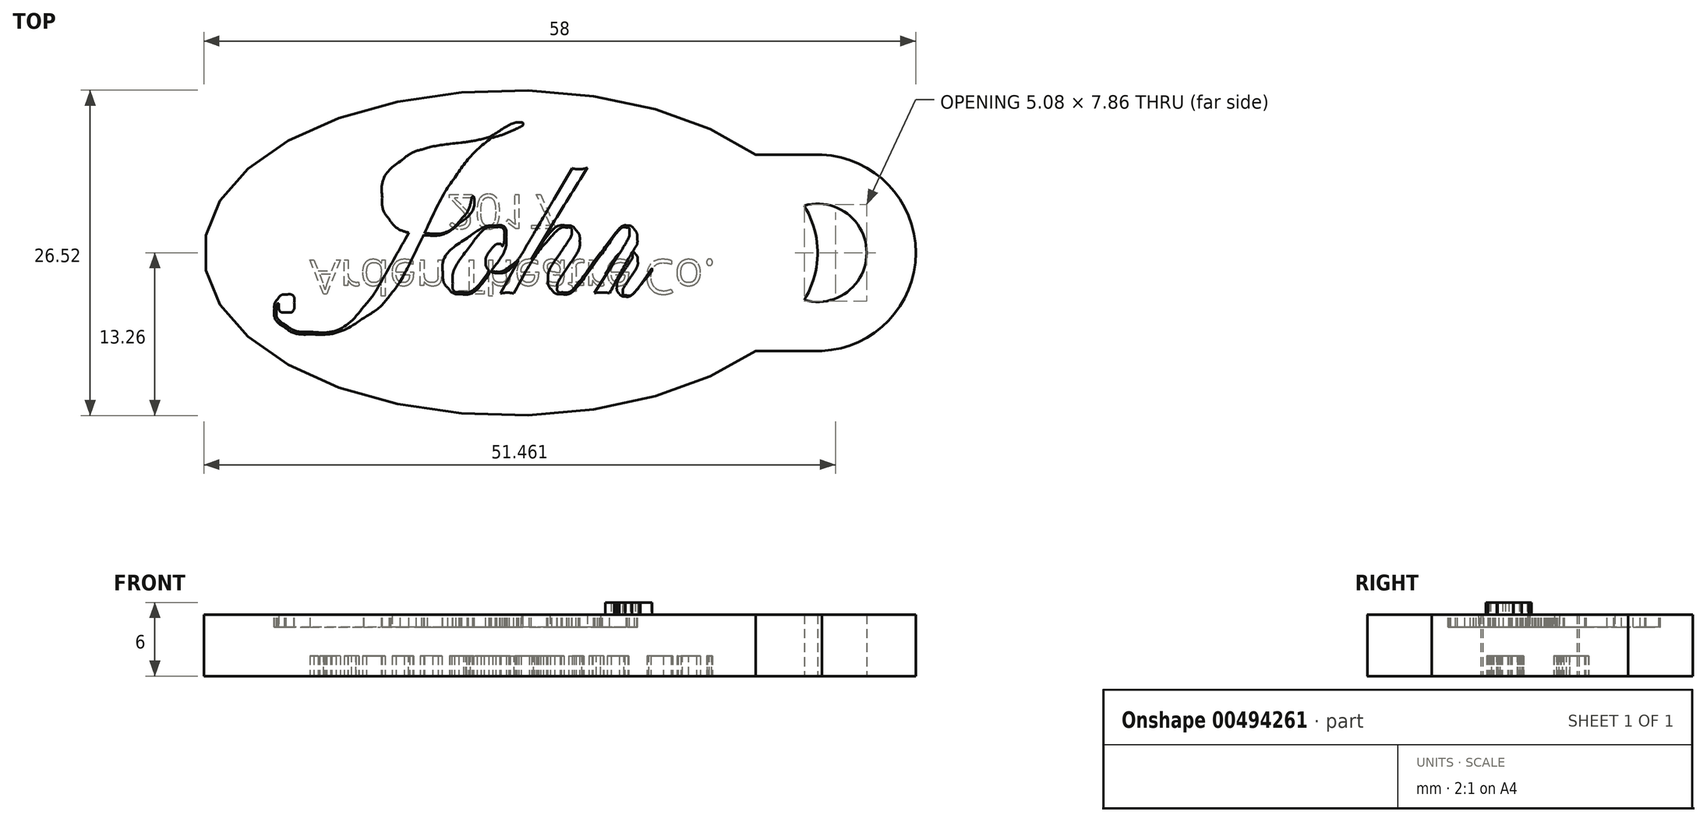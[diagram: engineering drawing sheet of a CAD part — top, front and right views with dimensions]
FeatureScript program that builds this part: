
annotation { "Feature Type Name" : "Feature", "Feature Type Description" : "" }
export const myFeature = defineFeature(function(context is Context, id is Id, definition is map)
    precondition{}
    {
        {
            var Q0;
            Q0=qCreatedBy(makeId("Top.planeOp"),FACE);
            var sketch = newSketch(context, id + "F0", { "sketchPlane" : qUnion([Q0])});
            skLineSegment(sketch, "E0", {"start": v(0, 0) * mm, "end": v(25, 0) * mm, "construction": true});
            skLineSegment(sketch, "E1", {"start": v(0, 0) * mm, "end": v(-25, 0) * mm, "construction": true});
            skEllipse(sketch, "E2", {"center": v(0, 0) * mm, "majorRadius": 25 * mm, "minorRadius": 13.26 * mm, "majorAxis": v(-1, 0)});
            skLineSegment(sketch, "E3", {"start": v(0, 0) * mm, "end": v(0, -13.26) * mm, "construction": true});
            skSolve(sketch);
        }
        {
            var Q0;
            Q0=makeQuery(id+"F0.imprint","IMPRINT",FACE,{"disambiguationData":[TD([[makeQuery(id+"F0.imprint","IMPRINT",EDGE,{"derivedFrom":sQuery(id+"F0.wireOp",EDGE,"E2")}),1.0]])]});
            extrude(context, id + "F1", {"entities" : qUnion([Q0]), "depth" : 5 * mm});
        }
        {
            var Q0;
            Q0=makeQuery(id+"F1.opExtrude","CAP_FACE",FACE,{"disambiguationData":[OSD([sQuery(id+"F0.wireOp",EDGE,"E2")])],"isStart":false});
            var sketch = newSketch(context, id + "F2", { "sketchPlane" : qUnion([Q0])});
            skFitSpline(sketch, "E4", {"points": [v(1.99, 5.68) * mm, v(1.99, 5.61) * mm, v(1.81, 5.5) * mm, v(1.46, 5.34) * mm]});
            skFitSpline(sketch, "E5", {"points": [v(1.46, 5.34) * mm, v(1.1, 5.18) * mm, v(0.7, 5.04) * mm, v(0.27, 4.92) * mm]});
            skFitSpline(sketch, "E6", {"points": [v(0.27, 4.92) * mm, v(-0.48, 4.3) * mm, v(-1.12, 3.61) * mm, v(-1.64, 2.87) * mm]});
            skFitSpline(sketch, "E7", {"points": [v(-1.64, 2.87) * mm, v(-2.16, 2.13) * mm, v(-2.73, 1.08) * mm, v(-3.36, -0.27) * mm]});
            skFitSpline(sketch, "E8", {"points": [v(-3.2, -0.27) * mm, v(-2.46, -0.27) * mm, v(-1.84, 0) * mm, v(-1.33, 0.55) * mm]});
            skFitSpline(sketch, "E9", {"points": [v(-1.33, 0.55) * mm, v(-1.08, 0.82) * mm, v(-0.9, 1.18) * mm, v(-0.8, 1.62) * mm]});
            skFitSpline(sketch, "E10", {"points": [v(-0.8, 1.62) * mm, v(-0.79, 1.7) * mm, v(-0.76, 1.73) * mm, v(-0.73, 1.73) * mm]});
            skFitSpline(sketch, "E11", {"points": [v(-0.73, 1.73) * mm, v(-0.69, 1.73) * mm, v(-0.67, 1.7) * mm, v(-0.67, 1.66) * mm]});
            skFitSpline(sketch, "E12", {"points": [v(-0.67, 1.66) * mm, v(-0.67, 1.17) * mm, v(-0.94, 0.7) * mm, v(-1.48, 0.27) * mm]});
            skFitSpline(sketch, "E13", {"points": [v(-1.48, 0.27) * mm, v(-2.01, -0.16) * mm, v(-2.58, -0.38) * mm, v(-3.18, -0.38) * mm]});
            skFitSpline(sketch, "E14", {"points": [v(-3.18, -0.38) * mm, v(-3.27, -0.38) * mm, v(-3.35, -0.37) * mm, v(-3.41, -0.36) * mm]});
            skFitSpline(sketch, "E15", {"points": [v(-3.41, -0.36) * mm, v(-3.44, -0.42) * mm, v(-3.57, -0.7) * mm, v(-3.8, -1.17) * mm]});
            skFitSpline(sketch, "E16", {"points": [v(-3.8, -1.17) * mm, v(-4.35, -2.29) * mm, v(-4.81, -3.09) * mm, v(-5.2, -3.57) * mm]});
            skFitSpline(sketch, "E17", {"points": [v(-5.2, -3.57) * mm, v(-5.56, -4.05) * mm, v(-6.05, -4.48) * mm, v(-6.64, -4.85) * mm]});
            skFitSpline(sketch, "E18", {"points": [v(-6.64, -4.85) * mm, v(-7.6, -5.45) * mm, v(-8.56, -5.75) * mm, v(-9.56, -5.75) * mm]});
            skFitSpline(sketch, "E19", {"points": [v(-9.56, -5.75) * mm, v(-10.13, -5.75) * mm, v(-10.6, -5.62) * mm, v(-10.97, -5.37) * mm]});
            skFitSpline(sketch, "E20", {"points": [v(-10.97, -5.37) * mm, v(-11.33, -5.1) * mm, v(-11.52, -4.78) * mm, v(-11.52, -4.38) * mm]});
            skFitSpline(sketch, "E21", {"points": [v(-11.52, -4.38) * mm, v(-11.52, -4.16) * mm, v(-11.45, -3.98) * mm, v(-11.33, -3.82) * mm]});
            skFitSpline(sketch, "E22", {"points": [v(-11.33, -3.82) * mm, v(-11.2, -3.67) * mm, v(-11.05, -3.6) * mm, v(-10.87, -3.6) * mm]});
            skFitSpline(sketch, "E23", {"points": [v(-10.87, -3.6) * mm, v(-10.59, -3.6) * mm, v(-10.44, -3.74) * mm, v(-10.44, -4.03) * mm]});
            skFitSpline(sketch, "E24", {"points": [v(-10.44, -4.03) * mm, v(-10.44, -4.38) * mm, v(-10.6, -4.56) * mm, v(-10.91, -4.56) * mm]});
            skFitSpline(sketch, "E25", {"points": [v(-10.91, -4.56) * mm, v(-11.14, -4.56) * mm, v(-11.26, -4.42) * mm, v(-11.28, -4.13) * mm]});
            skFitSpline(sketch, "E26", {"points": [v(-11.28, -4.13) * mm, v(-11.28, -4.11) * mm, v(-11.28, -4.1) * mm, v(-11.29, -4.09) * mm]});
            skFitSpline(sketch, "E27", {"points": [v(-11.29, -4.09) * mm, v(-11.36, -4.09) * mm, v(-11.4, -4.2) * mm, v(-11.4, -4.4) * mm]});
            skFitSpline(sketch, "E28", {"points": [v(-11.4, -4.4) * mm, v(-11.4, -4.75) * mm, v(-11.22, -5.03) * mm, v(-10.87, -5.27) * mm]});
            skFitSpline(sketch, "E29", {"points": [v(-10.87, -5.27) * mm, v(-10.53, -5.5) * mm, v(-10.1, -5.62) * mm, v(-9.57, -5.62) * mm]});
            skFitSpline(sketch, "E30", {"points": [v(-9.57, -5.62) * mm, v(-8.45, -5.62) * mm, v(-7.48, -5.16) * mm, v(-6.67, -4.25) * mm]});
            skFitSpline(sketch, "E31", {"points": [v(-6.67, -4.25) * mm, v(-6.35, -3.9) * mm, v(-6.04, -3.46) * mm, v(-5.75, -2.96) * mm]});
            skFitSpline(sketch, "E32", {"points": [v(-5.75, -2.96) * mm, v(-5.27, -2.11) * mm, v(-4.8, -1.27) * mm, v(-4.31, -0.42) * mm]});
            skLineSegment(sketch, "E33", {"start": v(-3.36, -0.27) * mm, "end": v(-3.2, -0.27) * mm});
            skFitSpline(sketch, "E34", {"points": [v(-4.2, -0.23) * mm, v(-4.65, -0.1) * mm, v(-5, 0.14) * mm, v(-5.26, 0.48) * mm]});
            skFitSpline(sketch, "E35", {"points": [v(-5.26, 0.48) * mm, v(-5.53, 0.83) * mm, v(-5.66, 1.22) * mm, v(-5.66, 1.66) * mm]});
            skFitSpline(sketch, "E36", {"points": [v(-5.66, 1.66) * mm, v(-5.66, 2.45) * mm, v(-5.33, 3.1) * mm, v(-4.68, 3.64) * mm]});
            skFitSpline(sketch, "E37", {"points": [v(-4.68, 3.64) * mm, v(-4.3, 3.95) * mm, v(-3.9, 4.17) * mm, v(-3.52, 4.29) * mm]});
            skFitSpline(sketch, "E38", {"points": [v(-3.52, 4.29) * mm, v(-3.12, 4.41) * mm, v(-2.42, 4.54) * mm, v(-1.4, 4.66) * mm]});
            skFitSpline(sketch, "E39", {"points": [v(-1.4, 4.66) * mm, v(-0.95, 4.72) * mm, v(-0.42, 4.82) * mm, v(0.2, 4.97) * mm]});
            skFitSpline(sketch, "E40", {"points": [v(0.2, 4.97) * mm, v(1.02, 5.5) * mm, v(1.58, 5.75) * mm, v(1.9, 5.75) * mm]});
            skFitSpline(sketch, "E41", {"points": [v(1.9, 5.75) * mm, v(1.96, 5.75) * mm, v(1.99, 5.73) * mm, v(1.99, 5.68) * mm]});
            skLineSegment(sketch, "E42", {"start": v(-4.31, -0.42) * mm, "end": v(-4.2, -0.23) * mm});
            skFitSpline(sketch, "E43", {"points": [v(0.08, 4.87) * mm, v(-0.22, 4.8) * mm, v(-0.62, 4.7) * mm, v(-1.13, 4.58) * mm]});
            skFitSpline(sketch, "E44", {"points": [v(-1.13, 4.58) * mm, v(-1.95, 4.4) * mm, v(-2.58, 4.22) * mm, v(-3, 4.04) * mm]});
            skFitSpline(sketch, "E45", {"points": [v(-3, 4.04) * mm, v(-3.43, 3.86) * mm, v(-3.83, 3.62) * mm, v(-4.18, 3.32) * mm]});
            skFitSpline(sketch, "E46", {"points": [v(-4.18, 3.32) * mm, v(-4.93, 2.67) * mm, v(-5.3, 2) * mm, v(-5.3, 1.29) * mm]});
            skFitSpline(sketch, "E47", {"points": [v(-5.3, 1.29) * mm, v(-5.3, 0.6) * mm, v(-4.92, 0.12) * mm, v(-4.15, -0.13) * mm]});
            skFitSpline(sketch, "E48", {"points": [v(-4.15, -0.13) * mm, v(-2.84, 2.24) * mm, v(-1.43, 3.9) * mm, v(0.08, 4.87) * mm]});
            skFitSpline(sketch, "E49", {"points": [v(2.03, -1.35) * mm, v(2.03, -1.42) * mm, v(1.9, -1.58) * mm, v(1.65, -1.84) * mm]});
            skFitSpline(sketch, "E50", {"points": [v(1.65, -1.84) * mm, v(1.26, -2.23) * mm, v(0.9, -2.42) * mm, v(0.58, -2.42) * mm]});
            skFitSpline(sketch, "E51", {"points": [v(0.58, -2.42) * mm, v(0.45, -2.42) * mm, v(0.33, -2.4) * mm, v(0.22, -2.34) * mm]});
            skFitSpline(sketch, "E52", {"points": [v(0.22, -2.34) * mm, v(-0.35, -3.16) * mm, v(-0.9, -3.57) * mm, v(-1.4, -3.57) * mm]});
            skFitSpline(sketch, "E53", {"points": [v(-1.4, -3.57) * mm, v(-1.67, -3.57) * mm, v(-1.9, -3.46) * mm, v(-2.08, -3.25) * mm]});
            skFitSpline(sketch, "E54", {"points": [v(-2.08, -3.25) * mm, v(-2.26, -3.03) * mm, v(-2.36, -2.77) * mm, v(-2.36, -2.46) * mm]});
            skFitSpline(sketch, "E55", {"points": [v(-2.36, -2.46) * mm, v(-2.36, -1.8) * mm, v(-1.91, -1.14) * mm, v(-1.03, -0.52) * mm]});
            skFitSpline(sketch, "E56", {"points": [v(-1.03, -0.52) * mm, v(-0.4, -0.07) * mm, v(0.1, 0.15) * mm, v(0.5, 0.15) * mm]});
            skFitSpline(sketch, "E57", {"points": [v(0.5, 0.15) * mm, v(0.88, 0.15) * mm, v(1.07, -0.05) * mm, v(1.07, -0.46) * mm]});
            skFitSpline(sketch, "E58", {"points": [v(1.07, -0.46) * mm, v(1.07, -0.96) * mm, v(0.8, -1.57) * mm, v(0.28, -2.27) * mm]});
            skFitSpline(sketch, "E59", {"points": [v(0.28, -2.27) * mm, v(0.36, -2.33) * mm, v(0.46, -2.35) * mm, v(0.57, -2.35) * mm]});
            skFitSpline(sketch, "E60", {"points": [v(0.57, -2.35) * mm, v(0.77, -2.35) * mm, v(1, -2.26) * mm, v(1.26, -2.08) * mm]});
            skFitSpline(sketch, "E61", {"points": [v(1.26, -2.08) * mm, v(1.52, -1.9) * mm, v(1.74, -1.67) * mm, v(1.9, -1.41) * mm]});
            skFitSpline(sketch, "E62", {"points": [v(1.9, -1.41) * mm, v(1.95, -1.35) * mm, v(1.99, -1.32) * mm, v(2, -1.32) * mm]});
            skFitSpline(sketch, "E63", {"points": [v(2, -1.32) * mm, v(2.03, -1.32) * mm, v(2.03, -1.33) * mm, v(2.03, -1.35) * mm]});
            skFitSpline(sketch, "E64", {"points": [v(0.97, -0.47) * mm, v(0.97, -0.11) * mm, v(0.81, 0.06) * mm, v(0.5, 0.06) * mm]});
            skFitSpline(sketch, "E65", {"points": [v(0.5, 0.06) * mm, v(0.1, 0.06) * mm, v(-0.4, -0.32) * mm, v(-0.96, -1.08) * mm]});
            skFitSpline(sketch, "E66", {"points": [v(-0.96, -1.08) * mm, v(-1.54, -1.84) * mm, v(-1.82, -2.48) * mm, v(-1.82, -3) * mm]});
            skFitSpline(sketch, "E67", {"points": [v(-1.82, -3) * mm, v(-1.82, -3.3) * mm, v(-1.68, -3.46) * mm, v(-1.4, -3.46) * mm]});
            skFitSpline(sketch, "E68", {"points": [v(-1.4, -3.46) * mm, v(-0.92, -3.46) * mm, v(-0.4, -3.07) * mm, v(0.16, -2.29) * mm]});
            skFitSpline(sketch, "E69", {"points": [v(0.16, -2.29) * mm, v(0.03, -2.15) * mm, v(-0.03, -2) * mm, v(-0.03, -1.85) * mm]});
            skFitSpline(sketch, "E70", {"points": [v(-0.03, -1.85) * mm, v(-0.03, -1.64) * mm, v(0.05, -1.42) * mm, v(0.22, -1.2) * mm]});
            skFitSpline(sketch, "E71", {"points": [v(0.22, -1.2) * mm, v(0.4, -0.96) * mm, v(0.56, -0.85) * mm, v(0.72, -0.85) * mm]});
            skFitSpline(sketch, "E72", {"points": [v(0.72, -0.85) * mm, v(0.8, -0.85) * mm, v(0.84, -0.9) * mm, v(0.87, -0.98) * mm]});
            skFitSpline(sketch, "E73", {"points": [v(0.87, -0.98) * mm, v(0.94, -0.83) * mm, v(0.97, -0.66) * mm, v(0.97, -0.47) * mm]});
            skFitSpline(sketch, "E74", {"points": [v(6.25, -1.35) * mm, v(6.25, -1.38) * mm, v(6.23, -1.42) * mm, v(6.19, -1.47) * mm]});
            skFitSpline(sketch, "E75", {"points": [v(5.9, -1.85) * mm, v(5.08, -3) * mm, v(4.47, -3.57) * mm, v(4.07, -3.57) * mm]});
            skFitSpline(sketch, "E76", {"points": [v(4.07, -3.57) * mm, v(3.86, -3.57) * mm, v(3.69, -3.5) * mm, v(3.55, -3.34) * mm]});
            skFitSpline(sketch, "E77", {"points": [v(3.55, -3.34) * mm, v(3.42, -3.2) * mm, v(3.35, -3) * mm, v(3.35, -2.77) * mm]});
            skFitSpline(sketch, "E78", {"points": [v(3.35, -2.77) * mm, v(3.35, -2.47) * mm, v(3.52, -2.07) * mm, v(3.85, -1.57) * mm]});
            skFitSpline(sketch, "E79", {"points": [v(3.85, -1.57) * mm, v(4.37, -0.8) * mm, v(4.63, -0.35) * mm, v(4.63, -0.2) * mm]});
            skFitSpline(sketch, "E80", {"points": [v(4.63, -0.2) * mm, v(4.63, -0.04) * mm, v(4.54, 0.05) * mm, v(4.36, 0.05) * mm]});
            skFitSpline(sketch, "E81", {"points": [v(4.36, 0.05) * mm, v(4.1, 0.05) * mm, v(3.74, -0.2) * mm, v(3.29, -0.73) * mm]});
            skFitSpline(sketch, "E82", {"points": [v(3.29, -0.73) * mm, v(2.85, -1.22) * mm, v(2.25, -2.16) * mm, v(1.48, -3.53) * mm]});
            skFitSpline(sketch, "E83", {"points": [v(1.48, -3.53) * mm, v(1.35, -3.5) * mm, v(1.24, -3.5) * mm, v(1.15, -3.5) * mm]});
            skFitSpline(sketch, "E84", {"points": [v(1.15, -3.5) * mm, v(1.05, -3.5) * mm, v(0.92, -3.5) * mm, v(0.76, -3.53) * mm]});
            skLineSegment(sketch, "E85", {"start": v(6.19, -1.47) * mm, "end": v(5.9, -1.85) * mm});
            skFitSpline(sketch, "E86", {"points": [v(1.73, -1.79) * mm, v(1.86, -1.54) * mm, v(2.06, -1.17) * mm, v(2.33, -0.69) * mm]});
            skFitSpline(sketch, "E87", {"points": [v(2.33, -0.69) * mm, v(2.47, -0.45) * mm, v(2.92, 0.3) * mm, v(3.66, 1.57) * mm]});
            skLineSegment(sketch, "E88", {"start": v(0.76, -3.53) * mm, "end": v(1.73, -1.79) * mm});
            skFitSpline(sketch, "E89", {"points": [v(4.66, 3.27) * mm, v(4.8, 3.24) * mm, v(4.9, 3.23) * mm, v(5, 3.23) * mm]});
            skFitSpline(sketch, "E90", {"points": [v(5, 3.23) * mm, v(5.17, 3.23) * mm, v(5.34, 3.25) * mm, v(5.5, 3.3) * mm]});
            skFitSpline(sketch, "E91", {"points": [v(5.5, 3.3) * mm, v(5.04, 2.56) * mm, v(4.36, 1.47) * mm, v(3.46, 0) * mm]});
            skFitSpline(sketch, "E92", {"points": [v(3.46, 0) * mm, v(3.43, -0.03) * mm, v(3.1, -0.6) * mm, v(2.44, -1.68) * mm]});
            skFitSpline(sketch, "E93", {"points": [v(2.44, -1.68) * mm, v(3.26, -0.46) * mm, v(3.91, 0.15) * mm, v(4.4, 0.15) * mm]});
            skFitSpline(sketch, "E94", {"points": [v(4.4, 0.15) * mm, v(4.58, 0.15) * mm, v(4.74, 0.07) * mm, v(4.87, -0.1) * mm]});
            skFitSpline(sketch, "E95", {"points": [v(4.87, -0.1) * mm, v(5, -0.26) * mm, v(5.07, -0.45) * mm, v(5.07, -0.69) * mm]});
            skFitSpline(sketch, "E96", {"points": [v(5.07, -0.69) * mm, v(5.07, -0.99) * mm, v(4.88, -1.42) * mm, v(4.5, -2) * mm]});
            skFitSpline(sketch, "E97", {"points": [v(4.5, -2) * mm, v(4.07, -2.63) * mm, v(3.85, -3.02) * mm, v(3.85, -3.19) * mm]});
            skFitSpline(sketch, "E98", {"points": [v(3.85, -3.19) * mm, v(3.85, -3.37) * mm, v(3.95, -3.47) * mm, v(4.13, -3.47) * mm]});
            skFitSpline(sketch, "E99", {"points": [v(4.13, -3.47) * mm, v(4.48, -3.47) * mm, v(5.04, -2.92) * mm, v(5.83, -1.81) * mm]});
            skLineSegment(sketch, "E100", {"start": v(3.66, 1.57) * mm, "end": v(4.66, 3.27) * mm});
            skFitSpline(sketch, "E101", {"points": [v(6.15, -1.39) * mm, v(6.17, -1.34) * mm, v(6.2, -1.32) * mm, v(6.23, -1.32) * mm]});
            skFitSpline(sketch, "E102", {"points": [v(6.23, -1.32) * mm, v(6.25, -1.32) * mm, v(6.25, -1.33) * mm, v(6.25, -1.35) * mm]});
            skLineSegment(sketch, "E103", {"start": v(5.83, -1.81) * mm, "end": v(6.03, -1.53) * mm});
            skLineSegment(sketch, "E104", {"start": v(6.03, -1.53) * mm, "end": v(6.15, -1.39) * mm});
            skFitSpline(sketch, "E105", {"points": [v(11.52, -1.36) * mm, v(11.52, -1.45) * mm, v(11.2, -1.88) * mm, v(10.57, -2.64) * mm]});
            skFitSpline(sketch, "E106", {"points": [v(10.57, -2.64) * mm, v(10.05, -3.26) * mm, v(9.64, -3.57) * mm, v(9.34, -3.57) * mm]});
            skFitSpline(sketch, "E107", {"points": [v(9.34, -3.57) * mm, v(9.14, -3.57) * mm, v(8.98, -3.5) * mm, v(8.84, -3.34) * mm]});
            skFitSpline(sketch, "E108", {"points": [v(8.84, -3.34) * mm, v(8.7, -3.18) * mm, v(8.64, -3) * mm, v(8.64, -2.77) * mm]});
            skFitSpline(sketch, "E109", {"points": [v(8.64, -2.77) * mm, v(8.64, -2.58) * mm, v(8.68, -2.4) * mm, v(8.76, -2.23) * mm]});
            skFitSpline(sketch, "E110", {"points": [v(8.76, -2.23) * mm, v(8.84, -2.06) * mm, v(9.06, -1.72) * mm, v(9.4, -1.22) * mm]});
            skFitSpline(sketch, "E111", {"points": [v(9.4, -1.22) * mm, v(9.75, -0.7) * mm, v(9.93, -0.36) * mm, v(9.93, -0.22) * mm]});
            skFitSpline(sketch, "E112", {"points": [v(9.93, -0.22) * mm, v(9.93, -0.04) * mm, v(9.84, 0.05) * mm, v(9.65, 0.05) * mm]});
            skFitSpline(sketch, "E113", {"points": [v(9.65, 0.05) * mm, v(9, 0.05) * mm, v(8.02, -1.14) * mm, v(6.7, -3.5) * mm]});
            skFitSpline(sketch, "E114", {"points": [v(6.7, -3.5) * mm, v(6.48, -3.5) * mm, v(6.35, -3.48) * mm, v(6.3, -3.48) * mm]});
            skFitSpline(sketch, "E115", {"points": [v(6.3, -3.48) * mm, v(6.15, -3.48) * mm, v(6, -3.5) * mm, v(5.87, -3.5) * mm]});
            skFitSpline(sketch, "E116", {"points": [v(6.9, -1.89) * mm, v(7.48, -0.96) * mm, v(7.77, -0.38) * mm, v(7.77, -0.15) * mm]});
            skFitSpline(sketch, "E117", {"points": [v(7.77, -0.15) * mm, v(7.77, -0.02) * mm, v(7.72, 0.05) * mm, v(7.6, 0.05) * mm]});
            skFitSpline(sketch, "E118", {"points": [v(7.6, 0.05) * mm, v(7.38, 0.05) * mm, v(6.94, -0.42) * mm, v(6.29, -1.36) * mm]});
            skFitSpline(sketch, "E119", {"points": [v(6.29, -1.36) * mm, v(6.25, -1.42) * mm, v(6.22, -1.45) * mm, v(6.2, -1.45) * mm]});
            skFitSpline(sketch, "E120", {"points": [v(6.2, -1.45) * mm, v(6.17, -1.45) * mm, v(6.16, -1.44) * mm, v(6.16, -1.41) * mm]});
            skFitSpline(sketch, "E121", {"points": [v(6.16, -1.41) * mm, v(6.16, -1.4) * mm, v(6.17, -1.37) * mm, v(6.18, -1.36) * mm]});
            skLineSegment(sketch, "E122", {"start": v(5.87, -3.5) * mm, "end": v(6.9, -1.89) * mm});
            skFitSpline(sketch, "E123", {"points": [v(6.3, -1.2) * mm, v(6.98, -0.3) * mm, v(7.43, 0.15) * mm, v(7.66, 0.15) * mm]});
            skFitSpline(sketch, "E124", {"points": [v(7.66, 0.15) * mm, v(7.8, 0.15) * mm, v(7.93, 0.08) * mm, v(8.04, -0.06) * mm]});
            skFitSpline(sketch, "E125", {"points": [v(8.04, -0.06) * mm, v(8.14, -0.2) * mm, v(8.2, -0.35) * mm, v(8.2, -0.54) * mm]});
            skFitSpline(sketch, "E126", {"points": [v(8.2, -0.54) * mm, v(8.2, -0.82) * mm, v(8.03, -1.21) * mm, v(7.7, -1.7) * mm]});
            skFitSpline(sketch, "E127", {"points": [v(7.7, -1.7) * mm, v(8.22, -1) * mm, v(8.62, -0.5) * mm, v(8.9, -0.25) * mm]});
            skFitSpline(sketch, "E128", {"points": [v(8.9, -0.25) * mm, v(9.17, 0.02) * mm, v(9.43, 0.15) * mm, v(9.67, 0.15) * mm]});
            skFitSpline(sketch, "E129", {"points": [v(9.67, 0.15) * mm, v(9.86, 0.15) * mm, v(10.02, 0.07) * mm, v(10.15, -0.09) * mm]});
            skFitSpline(sketch, "E130", {"points": [v(10.15, -0.09) * mm, v(10.28, -0.25) * mm, v(10.35, -0.44) * mm, v(10.35, -0.67) * mm]});
            skFitSpline(sketch, "E131", {"points": [v(10.35, -0.67) * mm, v(10.35, -0.97) * mm, v(10.15, -1.41) * mm, v(9.75, -2.02) * mm]});
            skFitSpline(sketch, "E132", {"points": [v(9.75, -2.02) * mm, v(9.33, -2.64) * mm, v(9.13, -3.03) * mm, v(9.13, -3.2) * mm]});
            skFitSpline(sketch, "E133", {"points": [v(9.13, -3.2) * mm, v(9.13, -3.38) * mm, v(9.22, -3.47) * mm, v(9.4, -3.47) * mm]});
            skFitSpline(sketch, "E134", {"points": [v(9.4, -3.47) * mm, v(9.79, -3.47) * mm, v(10.46, -2.78) * mm, v(11.41, -1.39) * mm]});
            skFitSpline(sketch, "E135", {"points": [v(11.41, -1.39) * mm, v(11.43, -1.34) * mm, v(11.46, -1.32) * mm, v(11.48, -1.32) * mm]});
            skFitSpline(sketch, "E136", {"points": [v(11.48, -1.32) * mm, v(11.5, -1.32) * mm, v(11.52, -1.34) * mm, v(11.52, -1.36) * mm]});
            skLineSegment(sketch, "E137", {"start": v(6.18, -1.36) * mm, "end": v(6.3, -1.2) * mm});
            skSolve(sketch);
        }
        {
            var Q0;
            Q0 = qSketchRegion(id + "F2", true);
            extrude(context, id + "F3", {"entities" : qUnion([Q0]), "depth" : 1 * mm});
        }
        {
            var Q0;
            Q0=makeQuery(id+"F3.opExtrude","SWEPT_BODY",BODY,{"disambiguationData":[OSD([sQuery(id+"F2.wireOp",EDGE,"E4"),sQuery(id+"F2.wireOp",EDGE,"E5"),sQuery(id+"F2.wireOp",EDGE,"E6"),sQuery(id+"F2.wireOp",EDGE,"E7"),sQuery(id+"F2.wireOp",EDGE,"E8"),sQuery(id+"F2.wireOp",EDGE,"E9"),sQuery(id+"F2.wireOp",EDGE,"E10"),sQuery(id+"F2.wireOp",EDGE,"E11"),sQuery(id+"F2.wireOp",EDGE,"E12"),sQuery(id+"F2.wireOp",EDGE,"E13"),sQuery(id+"F2.wireOp",EDGE,"E14"),sQuery(id+"F2.wireOp",EDGE,"E15"),sQuery(id+"F2.wireOp",EDGE,"E16"),sQuery(id+"F2.wireOp",EDGE,"E17"),sQuery(id+"F2.wireOp",EDGE,"E18"),sQuery(id+"F2.wireOp",EDGE,"E19"),sQuery(id+"F2.wireOp",EDGE,"E20"),sQuery(id+"F2.wireOp",EDGE,"E21"),sQuery(id+"F2.wireOp",EDGE,"E22"),sQuery(id+"F2.wireOp",EDGE,"E23"),sQuery(id+"F2.wireOp",EDGE,"E24"),sQuery(id+"F2.wireOp",EDGE,"E25"),sQuery(id+"F2.wireOp",EDGE,"E26"),sQuery(id+"F2.wireOp",EDGE,"E27"),sQuery(id+"F2.wireOp",EDGE,"E28"),sQuery(id+"F2.wireOp",EDGE,"E29"),sQuery(id+"F2.wireOp",EDGE,"E30"),sQuery(id+"F2.wireOp",EDGE,"E31"),sQuery(id+"F2.wireOp",EDGE,"E32"),sQuery(id+"F2.wireOp",EDGE,"E33"),sQuery(id+"F2.wireOp",EDGE,"E34"),sQuery(id+"F2.wireOp",EDGE,"E35"),sQuery(id+"F2.wireOp",EDGE,"E36"),sQuery(id+"F2.wireOp",EDGE,"E37"),sQuery(id+"F2.wireOp",EDGE,"E38"),sQuery(id+"F2.wireOp",EDGE,"E39"),sQuery(id+"F2.wireOp",EDGE,"E40"),sQuery(id+"F2.wireOp",EDGE,"E41"),sQuery(id+"F2.wireOp",EDGE,"E42"),sQuery(id+"F2.wireOp",EDGE,"E43"),sQuery(id+"F2.wireOp",EDGE,"E44"),sQuery(id+"F2.wireOp",EDGE,"E45"),sQuery(id+"F2.wireOp",EDGE,"E46"),sQuery(id+"F2.wireOp",EDGE,"E47"),sQuery(id+"F2.wireOp",EDGE,"E48")])]});
            var Q1;
            Q1=makeQuery(id+"F3.opExtrude","SWEPT_BODY",BODY,{"disambiguationData":[OSD([sQuery(id+"F2.wireOp",EDGE,"E49"),sQuery(id+"F2.wireOp",EDGE,"E50"),sQuery(id+"F2.wireOp",EDGE,"E51"),sQuery(id+"F2.wireOp",EDGE,"E52"),sQuery(id+"F2.wireOp",EDGE,"E53"),sQuery(id+"F2.wireOp",EDGE,"E54"),sQuery(id+"F2.wireOp",EDGE,"E55"),sQuery(id+"F2.wireOp",EDGE,"E56"),sQuery(id+"F2.wireOp",EDGE,"E57"),sQuery(id+"F2.wireOp",EDGE,"E58"),sQuery(id+"F2.wireOp",EDGE,"E59"),sQuery(id+"F2.wireOp",EDGE,"E60"),sQuery(id+"F2.wireOp",EDGE,"E61"),sQuery(id+"F2.wireOp",EDGE,"E62"),sQuery(id+"F2.wireOp",EDGE,"E64"),sQuery(id+"F2.wireOp",EDGE,"E65"),sQuery(id+"F2.wireOp",EDGE,"E66"),sQuery(id+"F2.wireOp",EDGE,"E67"),sQuery(id+"F2.wireOp",EDGE,"E68"),sQuery(id+"F2.wireOp",EDGE,"E69"),sQuery(id+"F2.wireOp",EDGE,"E70"),sQuery(id+"F2.wireOp",EDGE,"E71"),sQuery(id+"F2.wireOp",EDGE,"E72"),sQuery(id+"F2.wireOp",EDGE,"E73"),sQuery(id+"F2.wireOp",EDGE,"E74"),sQuery(id+"F2.wireOp",EDGE,"E75"),sQuery(id+"F2.wireOp",EDGE,"E76"),sQuery(id+"F2.wireOp",EDGE,"E77"),sQuery(id+"F2.wireOp",EDGE,"E78"),sQuery(id+"F2.wireOp",EDGE,"E79"),sQuery(id+"F2.wireOp",EDGE,"E80"),sQuery(id+"F2.wireOp",EDGE,"E81"),sQuery(id+"F2.wireOp",EDGE,"E82"),sQuery(id+"F2.wireOp",EDGE,"E83"),sQuery(id+"F2.wireOp",EDGE,"E84"),sQuery(id+"F2.wireOp",EDGE,"E85"),sQuery(id+"F2.wireOp",EDGE,"E86"),sQuery(id+"F2.wireOp",EDGE,"E87"),sQuery(id+"F2.wireOp",EDGE,"E88"),sQuery(id+"F2.wireOp",EDGE,"E89"),sQuery(id+"F2.wireOp",EDGE,"E90"),sQuery(id+"F2.wireOp",EDGE,"E91"),sQuery(id+"F2.wireOp",EDGE,"E92"),sQuery(id+"F2.wireOp",EDGE,"E93"),sQuery(id+"F2.wireOp",EDGE,"E94"),sQuery(id+"F2.wireOp",EDGE,"E95"),sQuery(id+"F2.wireOp",EDGE,"E96"),sQuery(id+"F2.wireOp",EDGE,"E97"),sQuery(id+"F2.wireOp",EDGE,"E98"),sQuery(id+"F2.wireOp",EDGE,"E99"),sQuery(id+"F2.wireOp",EDGE,"E100"),sQuery(id+"F2.wireOp",EDGE,"E101"),sQuery(id+"F2.wireOp",EDGE,"E103"),sQuery(id+"F2.wireOp",EDGE,"E104"),sQuery(id+"F2.wireOp",EDGE,"E105"),sQuery(id+"F2.wireOp",EDGE,"E106"),sQuery(id+"F2.wireOp",EDGE,"E107"),sQuery(id+"F2.wireOp",EDGE,"E108"),sQuery(id+"F2.wireOp",EDGE,"E109"),sQuery(id+"F2.wireOp",EDGE,"E110"),sQuery(id+"F2.wireOp",EDGE,"E111"),sQuery(id+"F2.wireOp",EDGE,"E112"),sQuery(id+"F2.wireOp",EDGE,"E113"),sQuery(id+"F2.wireOp",EDGE,"E114"),sQuery(id+"F2.wireOp",EDGE,"E115"),sQuery(id+"F2.wireOp",EDGE,"E116"),sQuery(id+"F2.wireOp",EDGE,"E117"),sQuery(id+"F2.wireOp",EDGE,"E118"),sQuery(id+"F2.wireOp",EDGE,"E119"),sQuery(id+"F2.wireOp",EDGE,"E122"),sQuery(id+"F2.wireOp",EDGE,"E123"),sQuery(id+"F2.wireOp",EDGE,"E124"),sQuery(id+"F2.wireOp",EDGE,"E125"),sQuery(id+"F2.wireOp",EDGE,"E126"),sQuery(id+"F2.wireOp",EDGE,"E127"),sQuery(id+"F2.wireOp",EDGE,"E128"),sQuery(id+"F2.wireOp",EDGE,"E129"),sQuery(id+"F2.wireOp",EDGE,"E130"),sQuery(id+"F2.wireOp",EDGE,"E131"),sQuery(id+"F2.wireOp",EDGE,"E132"),sQuery(id+"F2.wireOp",EDGE,"E133"),sQuery(id+"F2.wireOp",EDGE,"E134"),sQuery(id+"F2.wireOp",EDGE,"E135"),sQuery(id+"F2.wireOp",EDGE,"E136"),sQuery(id+"F2.wireOp",EDGE,"E137")])]});
            var Q2;
            Q2=qCreatedBy(makeId("Origin.pointOp"),VERTEX);
            transform(context, id + "F4", {"entities" : qUnion([Q0, Q1]), "transformType" : TransformType.SCALE_UNIFORMLY, "scale" : 1.5, "scalePoint" : qUnion([Q2]), "makeCopy" : false});
        }
        {
            var Q0;
            Q0=makeQuery(id+"F3.opExtrude","SWEPT_BODY",BODY,{"disambiguationData":[OSD([sQuery(id+"F2.wireOp",EDGE,"E4"),sQuery(id+"F2.wireOp",EDGE,"E5"),sQuery(id+"F2.wireOp",EDGE,"E6"),sQuery(id+"F2.wireOp",EDGE,"E7"),sQuery(id+"F2.wireOp",EDGE,"E8"),sQuery(id+"F2.wireOp",EDGE,"E9"),sQuery(id+"F2.wireOp",EDGE,"E10"),sQuery(id+"F2.wireOp",EDGE,"E11"),sQuery(id+"F2.wireOp",EDGE,"E12"),sQuery(id+"F2.wireOp",EDGE,"E13"),sQuery(id+"F2.wireOp",EDGE,"E14"),sQuery(id+"F2.wireOp",EDGE,"E15"),sQuery(id+"F2.wireOp",EDGE,"E16"),sQuery(id+"F2.wireOp",EDGE,"E17"),sQuery(id+"F2.wireOp",EDGE,"E18"),sQuery(id+"F2.wireOp",EDGE,"E19"),sQuery(id+"F2.wireOp",EDGE,"E20"),sQuery(id+"F2.wireOp",EDGE,"E21"),sQuery(id+"F2.wireOp",EDGE,"E22"),sQuery(id+"F2.wireOp",EDGE,"E23"),sQuery(id+"F2.wireOp",EDGE,"E24"),sQuery(id+"F2.wireOp",EDGE,"E25"),sQuery(id+"F2.wireOp",EDGE,"E26"),sQuery(id+"F2.wireOp",EDGE,"E27"),sQuery(id+"F2.wireOp",EDGE,"E28"),sQuery(id+"F2.wireOp",EDGE,"E29"),sQuery(id+"F2.wireOp",EDGE,"E30"),sQuery(id+"F2.wireOp",EDGE,"E31"),sQuery(id+"F2.wireOp",EDGE,"E32"),sQuery(id+"F2.wireOp",EDGE,"E33"),sQuery(id+"F2.wireOp",EDGE,"E34"),sQuery(id+"F2.wireOp",EDGE,"E35"),sQuery(id+"F2.wireOp",EDGE,"E36"),sQuery(id+"F2.wireOp",EDGE,"E37"),sQuery(id+"F2.wireOp",EDGE,"E38"),sQuery(id+"F2.wireOp",EDGE,"E39"),sQuery(id+"F2.wireOp",EDGE,"E40"),sQuery(id+"F2.wireOp",EDGE,"E41"),sQuery(id+"F2.wireOp",EDGE,"E42"),sQuery(id+"F2.wireOp",EDGE,"E43"),sQuery(id+"F2.wireOp",EDGE,"E44"),sQuery(id+"F2.wireOp",EDGE,"E45"),sQuery(id+"F2.wireOp",EDGE,"E46"),sQuery(id+"F2.wireOp",EDGE,"E47"),sQuery(id+"F2.wireOp",EDGE,"E48")])]});
            var Q1;
            Q1=makeQuery(id+"F3.opExtrude","SWEPT_BODY",BODY,{"disambiguationData":[OSD([sQuery(id+"F2.wireOp",EDGE,"E49"),sQuery(id+"F2.wireOp",EDGE,"E50"),sQuery(id+"F2.wireOp",EDGE,"E51"),sQuery(id+"F2.wireOp",EDGE,"E52"),sQuery(id+"F2.wireOp",EDGE,"E53"),sQuery(id+"F2.wireOp",EDGE,"E54"),sQuery(id+"F2.wireOp",EDGE,"E55"),sQuery(id+"F2.wireOp",EDGE,"E56"),sQuery(id+"F2.wireOp",EDGE,"E57"),sQuery(id+"F2.wireOp",EDGE,"E58"),sQuery(id+"F2.wireOp",EDGE,"E59"),sQuery(id+"F2.wireOp",EDGE,"E60"),sQuery(id+"F2.wireOp",EDGE,"E61"),sQuery(id+"F2.wireOp",EDGE,"E62"),sQuery(id+"F2.wireOp",EDGE,"E64"),sQuery(id+"F2.wireOp",EDGE,"E65"),sQuery(id+"F2.wireOp",EDGE,"E66"),sQuery(id+"F2.wireOp",EDGE,"E67"),sQuery(id+"F2.wireOp",EDGE,"E68"),sQuery(id+"F2.wireOp",EDGE,"E69"),sQuery(id+"F2.wireOp",EDGE,"E70"),sQuery(id+"F2.wireOp",EDGE,"E71"),sQuery(id+"F2.wireOp",EDGE,"E72"),sQuery(id+"F2.wireOp",EDGE,"E73"),sQuery(id+"F2.wireOp",EDGE,"E74"),sQuery(id+"F2.wireOp",EDGE,"E75"),sQuery(id+"F2.wireOp",EDGE,"E76"),sQuery(id+"F2.wireOp",EDGE,"E77"),sQuery(id+"F2.wireOp",EDGE,"E78"),sQuery(id+"F2.wireOp",EDGE,"E79"),sQuery(id+"F2.wireOp",EDGE,"E80"),sQuery(id+"F2.wireOp",EDGE,"E81"),sQuery(id+"F2.wireOp",EDGE,"E82"),sQuery(id+"F2.wireOp",EDGE,"E83"),sQuery(id+"F2.wireOp",EDGE,"E84"),sQuery(id+"F2.wireOp",EDGE,"E85"),sQuery(id+"F2.wireOp",EDGE,"E86"),sQuery(id+"F2.wireOp",EDGE,"E87"),sQuery(id+"F2.wireOp",EDGE,"E88"),sQuery(id+"F2.wireOp",EDGE,"E89"),sQuery(id+"F2.wireOp",EDGE,"E90"),sQuery(id+"F2.wireOp",EDGE,"E91"),sQuery(id+"F2.wireOp",EDGE,"E92"),sQuery(id+"F2.wireOp",EDGE,"E93"),sQuery(id+"F2.wireOp",EDGE,"E94"),sQuery(id+"F2.wireOp",EDGE,"E95"),sQuery(id+"F2.wireOp",EDGE,"E96"),sQuery(id+"F2.wireOp",EDGE,"E97"),sQuery(id+"F2.wireOp",EDGE,"E98"),sQuery(id+"F2.wireOp",EDGE,"E99"),sQuery(id+"F2.wireOp",EDGE,"E100"),sQuery(id+"F2.wireOp",EDGE,"E101"),sQuery(id+"F2.wireOp",EDGE,"E103"),sQuery(id+"F2.wireOp",EDGE,"E104"),sQuery(id+"F2.wireOp",EDGE,"E105"),sQuery(id+"F2.wireOp",EDGE,"E106"),sQuery(id+"F2.wireOp",EDGE,"E107"),sQuery(id+"F2.wireOp",EDGE,"E108"),sQuery(id+"F2.wireOp",EDGE,"E109"),sQuery(id+"F2.wireOp",EDGE,"E110"),sQuery(id+"F2.wireOp",EDGE,"E111"),sQuery(id+"F2.wireOp",EDGE,"E112"),sQuery(id+"F2.wireOp",EDGE,"E113"),sQuery(id+"F2.wireOp",EDGE,"E114"),sQuery(id+"F2.wireOp",EDGE,"E115"),sQuery(id+"F2.wireOp",EDGE,"E116"),sQuery(id+"F2.wireOp",EDGE,"E117"),sQuery(id+"F2.wireOp",EDGE,"E118"),sQuery(id+"F2.wireOp",EDGE,"E119"),sQuery(id+"F2.wireOp",EDGE,"E122"),sQuery(id+"F2.wireOp",EDGE,"E123"),sQuery(id+"F2.wireOp",EDGE,"E124"),sQuery(id+"F2.wireOp",EDGE,"E125"),sQuery(id+"F2.wireOp",EDGE,"E126"),sQuery(id+"F2.wireOp",EDGE,"E127"),sQuery(id+"F2.wireOp",EDGE,"E128"),sQuery(id+"F2.wireOp",EDGE,"E129"),sQuery(id+"F2.wireOp",EDGE,"E130"),sQuery(id+"F2.wireOp",EDGE,"E131"),sQuery(id+"F2.wireOp",EDGE,"E132"),sQuery(id+"F2.wireOp",EDGE,"E133"),sQuery(id+"F2.wireOp",EDGE,"E134"),sQuery(id+"F2.wireOp",EDGE,"E135"),sQuery(id+"F2.wireOp",EDGE,"E136"),sQuery(id+"F2.wireOp",EDGE,"E137")])]});
            transform(context, id + "F5", {"entities" : qUnion([Q0, Q1]), "transformType" : TransformType.TRANSLATION_3D, "dx" : -1.99 * mm, "dy" : 1.99 * mm, "dz" : 0 * mm, "makeCopy" : false});
        }
        {
            var Q0;
            Q0=makeQuery(id+"F3.opExtrude","CAP_FACE",FACE,{"disambiguationData":[OSD([sQuery(id+"F2.wireOp",EDGE,"E4"),sQuery(id+"F2.wireOp",EDGE,"E5"),sQuery(id+"F2.wireOp",EDGE,"E6"),sQuery(id+"F2.wireOp",EDGE,"E7"),sQuery(id+"F2.wireOp",EDGE,"E8"),sQuery(id+"F2.wireOp",EDGE,"E9"),sQuery(id+"F2.wireOp",EDGE,"E10"),sQuery(id+"F2.wireOp",EDGE,"E11"),sQuery(id+"F2.wireOp",EDGE,"E12"),sQuery(id+"F2.wireOp",EDGE,"E13"),sQuery(id+"F2.wireOp",EDGE,"E14"),sQuery(id+"F2.wireOp",EDGE,"E15"),sQuery(id+"F2.wireOp",EDGE,"E16"),sQuery(id+"F2.wireOp",EDGE,"E17"),sQuery(id+"F2.wireOp",EDGE,"E18"),sQuery(id+"F2.wireOp",EDGE,"E19"),sQuery(id+"F2.wireOp",EDGE,"E20"),sQuery(id+"F2.wireOp",EDGE,"E21"),sQuery(id+"F2.wireOp",EDGE,"E22"),sQuery(id+"F2.wireOp",EDGE,"E23"),sQuery(id+"F2.wireOp",EDGE,"E24"),sQuery(id+"F2.wireOp",EDGE,"E25"),sQuery(id+"F2.wireOp",EDGE,"E26"),sQuery(id+"F2.wireOp",EDGE,"E27"),sQuery(id+"F2.wireOp",EDGE,"E28"),sQuery(id+"F2.wireOp",EDGE,"E29"),sQuery(id+"F2.wireOp",EDGE,"E30"),sQuery(id+"F2.wireOp",EDGE,"E31"),sQuery(id+"F2.wireOp",EDGE,"E32"),sQuery(id+"F2.wireOp",EDGE,"E33"),sQuery(id+"F2.wireOp",EDGE,"E34"),sQuery(id+"F2.wireOp",EDGE,"E35"),sQuery(id+"F2.wireOp",EDGE,"E36"),sQuery(id+"F2.wireOp",EDGE,"E37"),sQuery(id+"F2.wireOp",EDGE,"E38"),sQuery(id+"F2.wireOp",EDGE,"E39"),sQuery(id+"F2.wireOp",EDGE,"E40"),sQuery(id+"F2.wireOp",EDGE,"E41"),sQuery(id+"F2.wireOp",EDGE,"E42"),sQuery(id+"F2.wireOp",EDGE,"E43"),sQuery(id+"F2.wireOp",EDGE,"E44"),sQuery(id+"F2.wireOp",EDGE,"E45"),sQuery(id+"F2.wireOp",EDGE,"E46"),sQuery(id+"F2.wireOp",EDGE,"E47"),sQuery(id+"F2.wireOp",EDGE,"E48")])],"isStart":false});
            var Q1;
            Q1=makeQuery(id+"F3.opExtrude","CAP_FACE",FACE,{"disambiguationData":[OSD([sQuery(id+"F2.wireOp",EDGE,"E49"),sQuery(id+"F2.wireOp",EDGE,"E50"),sQuery(id+"F2.wireOp",EDGE,"E51"),sQuery(id+"F2.wireOp",EDGE,"E52"),sQuery(id+"F2.wireOp",EDGE,"E53"),sQuery(id+"F2.wireOp",EDGE,"E54"),sQuery(id+"F2.wireOp",EDGE,"E55"),sQuery(id+"F2.wireOp",EDGE,"E56"),sQuery(id+"F2.wireOp",EDGE,"E57"),sQuery(id+"F2.wireOp",EDGE,"E58"),sQuery(id+"F2.wireOp",EDGE,"E59"),sQuery(id+"F2.wireOp",EDGE,"E60"),sQuery(id+"F2.wireOp",EDGE,"E61"),sQuery(id+"F2.wireOp",EDGE,"E62"),sQuery(id+"F2.wireOp",EDGE,"E64"),sQuery(id+"F2.wireOp",EDGE,"E65"),sQuery(id+"F2.wireOp",EDGE,"E66"),sQuery(id+"F2.wireOp",EDGE,"E67"),sQuery(id+"F2.wireOp",EDGE,"E68"),sQuery(id+"F2.wireOp",EDGE,"E69"),sQuery(id+"F2.wireOp",EDGE,"E70"),sQuery(id+"F2.wireOp",EDGE,"E71"),sQuery(id+"F2.wireOp",EDGE,"E72"),sQuery(id+"F2.wireOp",EDGE,"E73"),sQuery(id+"F2.wireOp",EDGE,"E74"),sQuery(id+"F2.wireOp",EDGE,"E75"),sQuery(id+"F2.wireOp",EDGE,"E76"),sQuery(id+"F2.wireOp",EDGE,"E77"),sQuery(id+"F2.wireOp",EDGE,"E78"),sQuery(id+"F2.wireOp",EDGE,"E79"),sQuery(id+"F2.wireOp",EDGE,"E80"),sQuery(id+"F2.wireOp",EDGE,"E81"),sQuery(id+"F2.wireOp",EDGE,"E82"),sQuery(id+"F2.wireOp",EDGE,"E83"),sQuery(id+"F2.wireOp",EDGE,"E84"),sQuery(id+"F2.wireOp",EDGE,"E85"),sQuery(id+"F2.wireOp",EDGE,"E86"),sQuery(id+"F2.wireOp",EDGE,"E87"),sQuery(id+"F2.wireOp",EDGE,"E88"),sQuery(id+"F2.wireOp",EDGE,"E89"),sQuery(id+"F2.wireOp",EDGE,"E90"),sQuery(id+"F2.wireOp",EDGE,"E91"),sQuery(id+"F2.wireOp",EDGE,"E92"),sQuery(id+"F2.wireOp",EDGE,"E93"),sQuery(id+"F2.wireOp",EDGE,"E94"),sQuery(id+"F2.wireOp",EDGE,"E95"),sQuery(id+"F2.wireOp",EDGE,"E96"),sQuery(id+"F2.wireOp",EDGE,"E97"),sQuery(id+"F2.wireOp",EDGE,"E98"),sQuery(id+"F2.wireOp",EDGE,"E99"),sQuery(id+"F2.wireOp",EDGE,"E100"),sQuery(id+"F2.wireOp",EDGE,"E101"),sQuery(id+"F2.wireOp",EDGE,"E103"),sQuery(id+"F2.wireOp",EDGE,"E104"),sQuery(id+"F2.wireOp",EDGE,"E105"),sQuery(id+"F2.wireOp",EDGE,"E106"),sQuery(id+"F2.wireOp",EDGE,"E107"),sQuery(id+"F2.wireOp",EDGE,"E108"),sQuery(id+"F2.wireOp",EDGE,"E109"),sQuery(id+"F2.wireOp",EDGE,"E110"),sQuery(id+"F2.wireOp",EDGE,"E111"),sQuery(id+"F2.wireOp",EDGE,"E112"),sQuery(id+"F2.wireOp",EDGE,"E113"),sQuery(id+"F2.wireOp",EDGE,"E114"),sQuery(id+"F2.wireOp",EDGE,"E115"),sQuery(id+"F2.wireOp",EDGE,"E116"),sQuery(id+"F2.wireOp",EDGE,"E117"),sQuery(id+"F2.wireOp",EDGE,"E118"),sQuery(id+"F2.wireOp",EDGE,"E119"),sQuery(id+"F2.wireOp",EDGE,"E122"),sQuery(id+"F2.wireOp",EDGE,"E123"),sQuery(id+"F2.wireOp",EDGE,"E124"),sQuery(id+"F2.wireOp",EDGE,"E125"),sQuery(id+"F2.wireOp",EDGE,"E126"),sQuery(id+"F2.wireOp",EDGE,"E127"),sQuery(id+"F2.wireOp",EDGE,"E128"),sQuery(id+"F2.wireOp",EDGE,"E129"),sQuery(id+"F2.wireOp",EDGE,"E130"),sQuery(id+"F2.wireOp",EDGE,"E131"),sQuery(id+"F2.wireOp",EDGE,"E132"),sQuery(id+"F2.wireOp",EDGE,"E133"),sQuery(id+"F2.wireOp",EDGE,"E134"),sQuery(id+"F2.wireOp",EDGE,"E135"),sQuery(id+"F2.wireOp",EDGE,"E136"),sQuery(id+"F2.wireOp",EDGE,"E137")])],"isStart":false});
            extrude(context, id + "F6", {"entities" : qUnion([Q0, Q1]), "operationType" : NewBodyOperationType.REMOVE, "oppositeDirection" : true, "depth" : 5 * mm});
        }
        {
            var Q0;
            Q0=qCreatedBy(makeId("Top.planeOp"),FACE);
            cPlane(context, id + "F7", {"entities" : qUnion([Q0]), "cplaneType" : CPlaneType.OFFSET, "offset" : 2.5 * mm, "width" : 150 * mm, "height" : 150 * mm});
        }
        {
            var Q0;
            Q0=qCreatedBy(id+"F7.planeOp",FACE);
            var sketch = newSketch(context, id + "F8", { "sketchPlane" : qUnion([Q0])});
            skLineSegment(sketch, "E138", {"start": v(0, 0) * mm, "end": v(25, 0) * mm, "construction": true});
            skCircle(sketch, "E139", {"center": v(25, 0) * mm, "radius": 4 * mm});
            skCircle(sketch, "E140.0", {"center": v(25, 0) * mm, "radius": 8 * mm});
            skLineSegment(sketch, "E141", {"start": v(25.34, 8) * mm, "end": v(19.76, 8) * mm});
            skLineSegment(sketch, "E142", {"start": v(25.34, 8) * mm, "end": v(25.34, -8) * mm});
            skLineSegment(sketch, "E143", {"start": v(19.76, 8) * mm, "end": v(19.76, -8) * mm});
            skLineSegment(sketch, "E144", {"start": v(25.34, -8) * mm, "end": v(19.76, -8) * mm});
            skSolve(sketch);
        }
        {
            var Q0;
            {var subQ0=sQuery(id+"F8.wireOp",EDGE,"E142");var subQ1=sQuery(id+"F8.wireOp",EDGE,"E139");var subQ2=makeQuery(id+"F8.imprint","INTERSECT",VERTEX,{"disambiguationData":[OD(0.0)],"derivedFrom":[subQ1,subQ0]});Q0=makeQuery(id+"F8.imprint","IMPRINT",FACE,{"disambiguationData":[TD([[makeQuery(id+"F8.imprint","IMPRINT",EDGE,{"disambiguationData":[TD([[subQ2,1.0]])],"derivedFrom":subQ1}),-1.0]])]});}
            var Q1;
            {var subQ0=sQuery(id+"F8.wireOp",EDGE,"E142");var subQ11=sQuery(id+"F8.wireOp",EDGE,"E139");var subQ12=makeQuery(id+"F8.imprint","INTERSECT",VERTEX,{"disambiguationData":[OD(0.0)],"derivedFrom":[subQ11,subQ0]});Q1=makeQuery(id+"F8.imprint","IMPRINT",FACE,{"disambiguationData":[TD([[makeQuery(id+"F8.imprint","IMPRINT",EDGE,{"disambiguationData":[TD([[subQ12,-1.0]])],"derivedFrom":subQ11}),-1.0]])]});}
            var Q2;
            {var subQ0=sQuery(id+"F8.wireOp",EDGE,"E141");var subQ1=sQuery(id+"F8.wireOp",EDGE,"E140.0");var subQ2=makeQuery(id+"F8.imprint","INTERSECT",VERTEX,{"derivedFrom":[subQ1,subQ0]});Q2=makeQuery(id+"F8.imprint","IMPRINT",FACE,{"disambiguationData":[TD([[makeQuery(id+"F8.imprint","IMPRINT",EDGE,{"disambiguationData":[TD([[subQ2,-1.0]])],"derivedFrom":subQ1}),-1.0]])]});}
            var Q3;
            {var subQ0=sQuery(id+"F8.wireOp",EDGE,"E143");var subQ1=sQuery(id+"F8.wireOp",EDGE,"E140.0");var subQ2=makeQuery(id+"F8.imprint","INTERSECT",VERTEX,{"disambiguationData":[OD(1.0)],"derivedFrom":[subQ1,subQ0]});Q3=makeQuery(id+"F8.imprint","IMPRINT",FACE,{"disambiguationData":[TD([[makeQuery(id+"F8.imprint","IMPRINT",EDGE,{"disambiguationData":[TD([[subQ2,-1.0]])],"derivedFrom":subQ1}),-1.0]])]});}
            extrude(context, id + "F9", {"entities" : qUnion([Q0, Q1, Q2, Q3]), "operationType" : NewBodyOperationType.ADD, "depth" : 2.5 * mm, "hasSecondDirection" : true, "secondDirectionOppositeDirection" : true, "secondDirectionDepth" : 2.5 * mm});
        }
        {
            var Q0;
            Q0=makeQuery(id+"F9.boolean.opBoolean","MERGE",FACE,{"derivedFrom":[makeQuery(id+"F1.opExtrude","CAP_FACE",FACE,{"disambiguationData":[OSD([sQuery(id+"F0.wireOp",EDGE,"E2")])],"isStart":true}),makeQuery(id+"F9.opExtrude","CAP_FACE",FACE,{"disambiguationData":[OSD([sQuery(id+"F8.wireOp",EDGE,"E139"),sQuery(id+"F8.wireOp",EDGE,"E140.0"),sQuery(id+"F8.wireOp",EDGE,"E141"),sQuery(id+"F8.wireOp",EDGE,"E143"),sQuery(id+"F8.wireOp",EDGE,"E144")])],"isStart":true})]});
            var sketch = newSketch(context, id + "F10", { "sketchPlane" : qUnion([Q0])});
            skText(sketch, "E145", { "text": "Arden Theatre Co.\n           2017", "fontName": "OpenSans-Regular.ttf"});
            const initialGuessF10  = {"E145": [-0.01172, -0.00347, 1, 0, 0.00805]};
            skSetInitialGuess(sketch, initialGuessF10);
            skSolve(sketch);
        }
        {
            var Q0;
            Q0 = qSketchRegion(id + "F10", true);
            extrude(context, id + "F11", {"entities" : qUnion([Q0]), "depth" : 1 * mm});
        }
        {
            var Q0;
            Q0=makeQuery(id+"F11.opExtrude","SWEPT_BODY",BODY,{"disambiguationData":[OSD([sQuery(id+"F10.wireOp",EDGE,"E145.sketch_text.stroke-0"),sQuery(id+"F10.wireOp",EDGE,"E145.sketch_text.stroke-1"),sQuery(id+"F10.wireOp",EDGE,"E145.sketch_text.stroke-2"),sQuery(id+"F10.wireOp",EDGE,"E145.sketch_text.stroke-3"),sQuery(id+"F10.wireOp",EDGE,"E145.sketch_text.stroke-4"),sQuery(id+"F10.wireOp",EDGE,"E145.sketch_text.stroke-5"),sQuery(id+"F10.wireOp",EDGE,"E145.sketch_text.stroke-6"),sQuery(id+"F10.wireOp",EDGE,"E145.sketch_text.stroke-7"),sQuery(id+"F10.wireOp",EDGE,"E145.sketch_text.stroke-8"),sQuery(id+"F10.wireOp",EDGE,"E145.sketch_text.stroke-9"),sQuery(id+"F10.wireOp",EDGE,"E145.sketch_text.stroke-10"),sQuery(id+"F10.wireOp",EDGE,"E145.sketch_text.stroke-11"),sQuery(id+"F10.wireOp",EDGE,"E145.sketch_text.stroke-12")])]});
            var Q1;
            Q1=makeQuery(id+"F11.opExtrude","SWEPT_BODY",BODY,{"disambiguationData":[OSD([sQuery(id+"F10.wireOp",EDGE,"E145.sketch_text.stroke-13"),sQuery(id+"F10.wireOp",EDGE,"E145.sketch_text.stroke-14"),sQuery(id+"F10.wireOp",EDGE,"E145.sketch_text.stroke-15"),sQuery(id+"F10.wireOp",EDGE,"E145.sketch_text.stroke-16"),sQuery(id+"F10.wireOp",EDGE,"E145.sketch_text.stroke-17"),sQuery(id+"F10.wireOp",EDGE,"E145.sketch_text.stroke-18"),sQuery(id+"F10.wireOp",EDGE,"E145.sketch_text.stroke-19"),sQuery(id+"F10.wireOp",EDGE,"E145.sketch_text.stroke-20"),sQuery(id+"F10.wireOp",EDGE,"E145.sketch_text.stroke-21"),sQuery(id+"F10.wireOp",EDGE,"E145.sketch_text.stroke-22"),sQuery(id+"F10.wireOp",EDGE,"E145.sketch_text.stroke-23"),sQuery(id+"F10.wireOp",EDGE,"E145.sketch_text.stroke-24"),sQuery(id+"F10.wireOp",EDGE,"E145.sketch_text.stroke-25")])]});
            var Q2;
            Q2=makeQuery(id+"F11.opExtrude","SWEPT_BODY",BODY,{"disambiguationData":[OSD([sQuery(id+"F10.wireOp",EDGE,"E145.sketch_text.stroke-26"),sQuery(id+"F10.wireOp",EDGE,"E145.sketch_text.stroke-27"),sQuery(id+"F10.wireOp",EDGE,"E145.sketch_text.stroke-28"),sQuery(id+"F10.wireOp",EDGE,"E145.sketch_text.stroke-29"),sQuery(id+"F10.wireOp",EDGE,"E145.sketch_text.stroke-30"),sQuery(id+"F10.wireOp",EDGE,"E145.sketch_text.stroke-31"),sQuery(id+"F10.wireOp",EDGE,"E145.sketch_text.stroke-32"),sQuery(id+"F10.wireOp",EDGE,"E145.sketch_text.stroke-33"),sQuery(id+"F10.wireOp",EDGE,"E145.sketch_text.stroke-34"),sQuery(id+"F10.wireOp",EDGE,"E145.sketch_text.stroke-35"),sQuery(id+"F10.wireOp",EDGE,"E145.sketch_text.stroke-36"),sQuery(id+"F10.wireOp",EDGE,"E145.sketch_text.stroke-37"),sQuery(id+"F10.wireOp",EDGE,"E145.sketch_text.stroke-38"),sQuery(id+"F10.wireOp",EDGE,"E145.sketch_text.stroke-39"),sQuery(id+"F10.wireOp",EDGE,"E145.sketch_text.stroke-40"),sQuery(id+"F10.wireOp",EDGE,"E145.sketch_text.stroke-41"),sQuery(id+"F10.wireOp",EDGE,"E145.sketch_text.stroke-42"),sQuery(id+"F10.wireOp",EDGE,"E145.sketch_text.stroke-43"),sQuery(id+"F10.wireOp",EDGE,"E145.sketch_text.stroke-44"),sQuery(id+"F10.wireOp",EDGE,"E145.sketch_text.stroke-45"),sQuery(id+"F10.wireOp",EDGE,"E145.sketch_text.stroke-46"),sQuery(id+"F10.wireOp",EDGE,"E145.sketch_text.stroke-47"),sQuery(id+"F10.wireOp",EDGE,"E145.sketch_text.stroke-48"),sQuery(id+"F10.wireOp",EDGE,"E145.sketch_text.stroke-49")])]});
            var Q3;
            Q3=makeQuery(id+"F11.opExtrude","SWEPT_BODY",BODY,{"disambiguationData":[OSD([sQuery(id+"F10.wireOp",EDGE,"E145.sketch_text.stroke-50"),sQuery(id+"F10.wireOp",EDGE,"E145.sketch_text.stroke-51"),sQuery(id+"F10.wireOp",EDGE,"E145.sketch_text.stroke-52"),sQuery(id+"F10.wireOp",EDGE,"E145.sketch_text.stroke-53"),sQuery(id+"F10.wireOp",EDGE,"E145.sketch_text.stroke-54"),sQuery(id+"F10.wireOp",EDGE,"E145.sketch_text.stroke-55"),sQuery(id+"F10.wireOp",EDGE,"E145.sketch_text.stroke-56"),sQuery(id+"F10.wireOp",EDGE,"E145.sketch_text.stroke-57"),sQuery(id+"F10.wireOp",EDGE,"E145.sketch_text.stroke-58"),sQuery(id+"F10.wireOp",EDGE,"E145.sketch_text.stroke-59"),sQuery(id+"F10.wireOp",EDGE,"E145.sketch_text.stroke-60"),sQuery(id+"F10.wireOp",EDGE,"E145.sketch_text.stroke-61"),sQuery(id+"F10.wireOp",EDGE,"E145.sketch_text.stroke-62"),sQuery(id+"F10.wireOp",EDGE,"E145.sketch_text.stroke-63"),sQuery(id+"F10.wireOp",EDGE,"E145.sketch_text.stroke-64"),sQuery(id+"F10.wireOp",EDGE,"E145.sketch_text.stroke-65"),sQuery(id+"F10.wireOp",EDGE,"E145.sketch_text.stroke-66"),sQuery(id+"F10.wireOp",EDGE,"E145.sketch_text.stroke-67"),sQuery(id+"F10.wireOp",EDGE,"E145.sketch_text.stroke-68")])]});
            var Q4;
            Q4=makeQuery(id+"F11.opExtrude","SWEPT_BODY",BODY,{"disambiguationData":[OSD([sQuery(id+"F10.wireOp",EDGE,"E145.sketch_text.stroke-69"),sQuery(id+"F10.wireOp",EDGE,"E145.sketch_text.stroke-70"),sQuery(id+"F10.wireOp",EDGE,"E145.sketch_text.stroke-71"),sQuery(id+"F10.wireOp",EDGE,"E145.sketch_text.stroke-72"),sQuery(id+"F10.wireOp",EDGE,"E145.sketch_text.stroke-73"),sQuery(id+"F10.wireOp",EDGE,"E145.sketch_text.stroke-74"),sQuery(id+"F10.wireOp",EDGE,"E145.sketch_text.stroke-75"),sQuery(id+"F10.wireOp",EDGE,"E145.sketch_text.stroke-76"),sQuery(id+"F10.wireOp",EDGE,"E145.sketch_text.stroke-77"),sQuery(id+"F10.wireOp",EDGE,"E145.sketch_text.stroke-78"),sQuery(id+"F10.wireOp",EDGE,"E145.sketch_text.stroke-79"),sQuery(id+"F10.wireOp",EDGE,"E145.sketch_text.stroke-80"),sQuery(id+"F10.wireOp",EDGE,"E145.sketch_text.stroke-81"),sQuery(id+"F10.wireOp",EDGE,"E145.sketch_text.stroke-82"),sQuery(id+"F10.wireOp",EDGE,"E145.sketch_text.stroke-83"),sQuery(id+"F10.wireOp",EDGE,"E145.sketch_text.stroke-84"),sQuery(id+"F10.wireOp",EDGE,"E145.sketch_text.stroke-85")])]});
            var Q5;
            Q5=makeQuery(id+"F11.opExtrude","SWEPT_BODY",BODY,{"disambiguationData":[OSD([sQuery(id+"F10.wireOp",EDGE,"E145.sketch_text.stroke-86"),sQuery(id+"F10.wireOp",EDGE,"E145.sketch_text.stroke-87"),sQuery(id+"F10.wireOp",EDGE,"E145.sketch_text.stroke-88"),sQuery(id+"F10.wireOp",EDGE,"E145.sketch_text.stroke-89"),sQuery(id+"F10.wireOp",EDGE,"E145.sketch_text.stroke-90"),sQuery(id+"F10.wireOp",EDGE,"E145.sketch_text.stroke-91"),sQuery(id+"F10.wireOp",EDGE,"E145.sketch_text.stroke-92"),sQuery(id+"F10.wireOp",EDGE,"E145.sketch_text.stroke-93")])]});
            var Q6;
            Q6=makeQuery(id+"F11.opExtrude","SWEPT_BODY",BODY,{"disambiguationData":[OSD([sQuery(id+"F10.wireOp",EDGE,"E145.sketch_text.stroke-94"),sQuery(id+"F10.wireOp",EDGE,"E145.sketch_text.stroke-95"),sQuery(id+"F10.wireOp",EDGE,"E145.sketch_text.stroke-96"),sQuery(id+"F10.wireOp",EDGE,"E145.sketch_text.stroke-97"),sQuery(id+"F10.wireOp",EDGE,"E145.sketch_text.stroke-98"),sQuery(id+"F10.wireOp",EDGE,"E145.sketch_text.stroke-99"),sQuery(id+"F10.wireOp",EDGE,"E145.sketch_text.stroke-100"),sQuery(id+"F10.wireOp",EDGE,"E145.sketch_text.stroke-101"),sQuery(id+"F10.wireOp",EDGE,"E145.sketch_text.stroke-102"),sQuery(id+"F10.wireOp",EDGE,"E145.sketch_text.stroke-103"),sQuery(id+"F10.wireOp",EDGE,"E145.sketch_text.stroke-104"),sQuery(id+"F10.wireOp",EDGE,"E145.sketch_text.stroke-105"),sQuery(id+"F10.wireOp",EDGE,"E145.sketch_text.stroke-106"),sQuery(id+"F10.wireOp",EDGE,"E145.sketch_text.stroke-107"),sQuery(id+"F10.wireOp",EDGE,"E145.sketch_text.stroke-108"),sQuery(id+"F10.wireOp",EDGE,"E145.sketch_text.stroke-109"),sQuery(id+"F10.wireOp",EDGE,"E145.sketch_text.stroke-110"),sQuery(id+"F10.wireOp",EDGE,"E145.sketch_text.stroke-111")])]});
            var Q7;
            Q7=makeQuery(id+"F11.opExtrude","SWEPT_BODY",BODY,{"disambiguationData":[OSD([sQuery(id+"F10.wireOp",EDGE,"E145.sketch_text.stroke-112"),sQuery(id+"F10.wireOp",EDGE,"E145.sketch_text.stroke-113"),sQuery(id+"F10.wireOp",EDGE,"E145.sketch_text.stroke-114"),sQuery(id+"F10.wireOp",EDGE,"E145.sketch_text.stroke-115"),sQuery(id+"F10.wireOp",EDGE,"E145.sketch_text.stroke-116"),sQuery(id+"F10.wireOp",EDGE,"E145.sketch_text.stroke-117"),sQuery(id+"F10.wireOp",EDGE,"E145.sketch_text.stroke-118"),sQuery(id+"F10.wireOp",EDGE,"E145.sketch_text.stroke-119"),sQuery(id+"F10.wireOp",EDGE,"E145.sketch_text.stroke-120"),sQuery(id+"F10.wireOp",EDGE,"E145.sketch_text.stroke-121"),sQuery(id+"F10.wireOp",EDGE,"E145.sketch_text.stroke-122"),sQuery(id+"F10.wireOp",EDGE,"E145.sketch_text.stroke-123"),sQuery(id+"F10.wireOp",EDGE,"E145.sketch_text.stroke-124"),sQuery(id+"F10.wireOp",EDGE,"E145.sketch_text.stroke-125"),sQuery(id+"F10.wireOp",EDGE,"E145.sketch_text.stroke-126"),sQuery(id+"F10.wireOp",EDGE,"E145.sketch_text.stroke-127"),sQuery(id+"F10.wireOp",EDGE,"E145.sketch_text.stroke-128"),sQuery(id+"F10.wireOp",EDGE,"E145.sketch_text.stroke-129"),sQuery(id+"F10.wireOp",EDGE,"E145.sketch_text.stroke-130")])]});
            var Q8;
            Q8=makeQuery(id+"F11.opExtrude","SWEPT_BODY",BODY,{"disambiguationData":[OSD([sQuery(id+"F10.wireOp",EDGE,"E145.sketch_text.stroke-158"),sQuery(id+"F10.wireOp",EDGE,"E145.sketch_text.stroke-159"),sQuery(id+"F10.wireOp",EDGE,"E145.sketch_text.stroke-160"),sQuery(id+"F10.wireOp",EDGE,"E145.sketch_text.stroke-161"),sQuery(id+"F10.wireOp",EDGE,"E145.sketch_text.stroke-162"),sQuery(id+"F10.wireOp",EDGE,"E145.sketch_text.stroke-163"),sQuery(id+"F10.wireOp",EDGE,"E145.sketch_text.stroke-164"),sQuery(id+"F10.wireOp",EDGE,"E145.sketch_text.stroke-165"),sQuery(id+"F10.wireOp",EDGE,"E145.sketch_text.stroke-166"),sQuery(id+"F10.wireOp",EDGE,"E145.sketch_text.stroke-167"),sQuery(id+"F10.wireOp",EDGE,"E145.sketch_text.stroke-168"),sQuery(id+"F10.wireOp",EDGE,"E145.sketch_text.stroke-169"),sQuery(id+"F10.wireOp",EDGE,"E145.sketch_text.stroke-170"),sQuery(id+"F10.wireOp",EDGE,"E145.sketch_text.stroke-171"),sQuery(id+"F10.wireOp",EDGE,"E145.sketch_text.stroke-172"),sQuery(id+"F10.wireOp",EDGE,"E145.sketch_text.stroke-173"),sQuery(id+"F10.wireOp",EDGE,"E145.sketch_text.stroke-174"),sQuery(id+"F10.wireOp",EDGE,"E145.sketch_text.stroke-175"),sQuery(id+"F10.wireOp",EDGE,"E145.sketch_text.stroke-176")])]});
            var Q9;
            Q9=makeQuery(id+"F11.opExtrude","SWEPT_BODY",BODY,{"disambiguationData":[OSD([sQuery(id+"F10.wireOp",EDGE,"E145.sketch_text.stroke-131"),sQuery(id+"F10.wireOp",EDGE,"E145.sketch_text.stroke-132"),sQuery(id+"F10.wireOp",EDGE,"E145.sketch_text.stroke-133"),sQuery(id+"F10.wireOp",EDGE,"E145.sketch_text.stroke-134"),sQuery(id+"F10.wireOp",EDGE,"E145.sketch_text.stroke-135"),sQuery(id+"F10.wireOp",EDGE,"E145.sketch_text.stroke-136"),sQuery(id+"F10.wireOp",EDGE,"E145.sketch_text.stroke-137"),sQuery(id+"F10.wireOp",EDGE,"E145.sketch_text.stroke-138"),sQuery(id+"F10.wireOp",EDGE,"E145.sketch_text.stroke-139"),sQuery(id+"F10.wireOp",EDGE,"E145.sketch_text.stroke-140"),sQuery(id+"F10.wireOp",EDGE,"E145.sketch_text.stroke-141"),sQuery(id+"F10.wireOp",EDGE,"E145.sketch_text.stroke-142"),sQuery(id+"F10.wireOp",EDGE,"E145.sketch_text.stroke-143"),sQuery(id+"F10.wireOp",EDGE,"E145.sketch_text.stroke-144"),sQuery(id+"F10.wireOp",EDGE,"E145.sketch_text.stroke-145"),sQuery(id+"F10.wireOp",EDGE,"E145.sketch_text.stroke-146"),sQuery(id+"F10.wireOp",EDGE,"E145.sketch_text.stroke-147"),sQuery(id+"F10.wireOp",EDGE,"E145.sketch_text.stroke-148"),sQuery(id+"F10.wireOp",EDGE,"E145.sketch_text.stroke-149"),sQuery(id+"F10.wireOp",EDGE,"E145.sketch_text.stroke-150"),sQuery(id+"F10.wireOp",EDGE,"E145.sketch_text.stroke-151"),sQuery(id+"F10.wireOp",EDGE,"E145.sketch_text.stroke-152"),sQuery(id+"F10.wireOp",EDGE,"E145.sketch_text.stroke-153"),sQuery(id+"F10.wireOp",EDGE,"E145.sketch_text.stroke-154"),sQuery(id+"F10.wireOp",EDGE,"E145.sketch_text.stroke-155"),sQuery(id+"F10.wireOp",EDGE,"E145.sketch_text.stroke-156"),sQuery(id+"F10.wireOp",EDGE,"E145.sketch_text.stroke-157")])]});
            var Q10;
            Q10=makeQuery(id+"F11.opExtrude","SWEPT_BODY",BODY,{"disambiguationData":[OSD([sQuery(id+"F10.wireOp",EDGE,"E145.sketch_text.stroke-177"),sQuery(id+"F10.wireOp",EDGE,"E145.sketch_text.stroke-178"),sQuery(id+"F10.wireOp",EDGE,"E145.sketch_text.stroke-179"),sQuery(id+"F10.wireOp",EDGE,"E145.sketch_text.stroke-180"),sQuery(id+"F10.wireOp",EDGE,"E145.sketch_text.stroke-181"),sQuery(id+"F10.wireOp",EDGE,"E145.sketch_text.stroke-182"),sQuery(id+"F10.wireOp",EDGE,"E145.sketch_text.stroke-183"),sQuery(id+"F10.wireOp",EDGE,"E145.sketch_text.stroke-184"),sQuery(id+"F10.wireOp",EDGE,"E145.sketch_text.stroke-185"),sQuery(id+"F10.wireOp",EDGE,"E145.sketch_text.stroke-186"),sQuery(id+"F10.wireOp",EDGE,"E145.sketch_text.stroke-187"),sQuery(id+"F10.wireOp",EDGE,"E145.sketch_text.stroke-188"),sQuery(id+"F10.wireOp",EDGE,"E145.sketch_text.stroke-189")])]});
            var Q11;
            Q11=makeQuery(id+"F11.opExtrude","SWEPT_BODY",BODY,{"disambiguationData":[OSD([sQuery(id+"F10.wireOp",EDGE,"E145.sketch_text.stroke-190"),sQuery(id+"F10.wireOp",EDGE,"E145.sketch_text.stroke-191"),sQuery(id+"F10.wireOp",EDGE,"E145.sketch_text.stroke-192"),sQuery(id+"F10.wireOp",EDGE,"E145.sketch_text.stroke-193"),sQuery(id+"F10.wireOp",EDGE,"E145.sketch_text.stroke-194"),sQuery(id+"F10.wireOp",EDGE,"E145.sketch_text.stroke-195"),sQuery(id+"F10.wireOp",EDGE,"E145.sketch_text.stroke-196"),sQuery(id+"F10.wireOp",EDGE,"E145.sketch_text.stroke-197"),sQuery(id+"F10.wireOp",EDGE,"E145.sketch_text.stroke-198"),sQuery(id+"F10.wireOp",EDGE,"E145.sketch_text.stroke-199"),sQuery(id+"F10.wireOp",EDGE,"E145.sketch_text.stroke-200"),sQuery(id+"F10.wireOp",EDGE,"E145.sketch_text.stroke-201"),sQuery(id+"F10.wireOp",EDGE,"E145.sketch_text.stroke-202"),sQuery(id+"F10.wireOp",EDGE,"E145.sketch_text.stroke-203"),sQuery(id+"F10.wireOp",EDGE,"E145.sketch_text.stroke-204"),sQuery(id+"F10.wireOp",EDGE,"E145.sketch_text.stroke-205"),sQuery(id+"F10.wireOp",EDGE,"E145.sketch_text.stroke-206"),sQuery(id+"F10.wireOp",EDGE,"E145.sketch_text.stroke-207"),sQuery(id+"F10.wireOp",EDGE,"E145.sketch_text.stroke-208")])]});
            var Q12;
            Q12=makeQuery(id+"F11.opExtrude","SWEPT_BODY",BODY,{"disambiguationData":[OSD([sQuery(id+"F10.wireOp",EDGE,"E145.sketch_text.stroke-209"),sQuery(id+"F10.wireOp",EDGE,"E145.sketch_text.stroke-210"),sQuery(id+"F10.wireOp",EDGE,"E145.sketch_text.stroke-211"),sQuery(id+"F10.wireOp",EDGE,"E145.sketch_text.stroke-212"),sQuery(id+"F10.wireOp",EDGE,"E145.sketch_text.stroke-213"),sQuery(id+"F10.wireOp",EDGE,"E145.sketch_text.stroke-214"),sQuery(id+"F10.wireOp",EDGE,"E145.sketch_text.stroke-215"),sQuery(id+"F10.wireOp",EDGE,"E145.sketch_text.stroke-216"),sQuery(id+"F10.wireOp",EDGE,"E145.sketch_text.stroke-217"),sQuery(id+"F10.wireOp",EDGE,"E145.sketch_text.stroke-218"),sQuery(id+"F10.wireOp",EDGE,"E145.sketch_text.stroke-219"),sQuery(id+"F10.wireOp",EDGE,"E145.sketch_text.stroke-220"),sQuery(id+"F10.wireOp",EDGE,"E145.sketch_text.stroke-221"),sQuery(id+"F10.wireOp",EDGE,"E145.sketch_text.stroke-222"),sQuery(id+"F10.wireOp",EDGE,"E145.sketch_text.stroke-223")])]});
            var Q13;
            Q13=makeQuery(id+"F11.opExtrude","SWEPT_BODY",BODY,{"disambiguationData":[OSD([sQuery(id+"F10.wireOp",EDGE,"E145.sketch_text.stroke-224"),sQuery(id+"F10.wireOp",EDGE,"E145.sketch_text.stroke-225"),sQuery(id+"F10.wireOp",EDGE,"E145.sketch_text.stroke-226"),sQuery(id+"F10.wireOp",EDGE,"E145.sketch_text.stroke-227"),sQuery(id+"F10.wireOp",EDGE,"E145.sketch_text.stroke-228"),sQuery(id+"F10.wireOp",EDGE,"E145.sketch_text.stroke-229"),sQuery(id+"F10.wireOp",EDGE,"E145.sketch_text.stroke-230"),sQuery(id+"F10.wireOp",EDGE,"E145.sketch_text.stroke-231"),sQuery(id+"F10.wireOp",EDGE,"E145.sketch_text.stroke-232"),sQuery(id+"F10.wireOp",EDGE,"E145.sketch_text.stroke-233"),sQuery(id+"F10.wireOp",EDGE,"E145.sketch_text.stroke-234"),sQuery(id+"F10.wireOp",EDGE,"E145.sketch_text.stroke-235"),sQuery(id+"F10.wireOp",EDGE,"E145.sketch_text.stroke-236"),sQuery(id+"F10.wireOp",EDGE,"E145.sketch_text.stroke-237"),sQuery(id+"F10.wireOp",EDGE,"E145.sketch_text.stroke-238"),sQuery(id+"F10.wireOp",EDGE,"E145.sketch_text.stroke-239"),sQuery(id+"F10.wireOp",EDGE,"E145.sketch_text.stroke-240")])]});
            var Q14;
            Q14=makeQuery(id+"F11.opExtrude","SWEPT_BODY",BODY,{"disambiguationData":[OSD([sQuery(id+"F10.wireOp",EDGE,"E145.sketch_text.stroke-249"),sQuery(id+"F10.wireOp",EDGE,"E145.sketch_text.stroke-250"),sQuery(id+"F10.wireOp",EDGE,"E145.sketch_text.stroke-251"),sQuery(id+"F10.wireOp",EDGE,"E145.sketch_text.stroke-252"),sQuery(id+"F10.wireOp",EDGE,"E145.sketch_text.stroke-253"),sQuery(id+"F10.wireOp",EDGE,"E145.sketch_text.stroke-254"),sQuery(id+"F10.wireOp",EDGE,"E145.sketch_text.stroke-255"),sQuery(id+"F10.wireOp",EDGE,"E145.sketch_text.stroke-256"),sQuery(id+"F10.wireOp",EDGE,"E145.sketch_text.stroke-257"),sQuery(id+"F10.wireOp",EDGE,"E145.sketch_text.stroke-258"),sQuery(id+"F10.wireOp",EDGE,"E145.sketch_text.stroke-259"),sQuery(id+"F10.wireOp",EDGE,"E145.sketch_text.stroke-260"),sQuery(id+"F10.wireOp",EDGE,"E145.sketch_text.stroke-261"),sQuery(id+"F10.wireOp",EDGE,"E145.sketch_text.stroke-262"),sQuery(id+"F10.wireOp",EDGE,"E145.sketch_text.stroke-263"),sQuery(id+"F10.wireOp",EDGE,"E145.sketch_text.stroke-264"),sQuery(id+"F10.wireOp",EDGE,"E145.sketch_text.stroke-265"),sQuery(id+"F10.wireOp",EDGE,"E145.sketch_text.stroke-266"),sQuery(id+"F10.wireOp",EDGE,"E145.sketch_text.stroke-267"),sQuery(id+"F10.wireOp",EDGE,"E145.sketch_text.stroke-268")])]});
            var Q15;
            Q15=makeQuery(id+"F11.opExtrude","SWEPT_BODY",BODY,{"disambiguationData":[OSD([sQuery(id+"F10.wireOp",EDGE,"E145.sketch_text.stroke-241"),sQuery(id+"F10.wireOp",EDGE,"E145.sketch_text.stroke-242"),sQuery(id+"F10.wireOp",EDGE,"E145.sketch_text.stroke-243"),sQuery(id+"F10.wireOp",EDGE,"E145.sketch_text.stroke-244"),sQuery(id+"F10.wireOp",EDGE,"E145.sketch_text.stroke-245"),sQuery(id+"F10.wireOp",EDGE,"E145.sketch_text.stroke-246"),sQuery(id+"F10.wireOp",EDGE,"E145.sketch_text.stroke-247"),sQuery(id+"F10.wireOp",EDGE,"E145.sketch_text.stroke-248")])]});
            var Q16;
            Q16=makeQuery(id+"F11.opExtrude","SWEPT_BODY",BODY,{"disambiguationData":[OSD([sQuery(id+"F10.wireOp",EDGE,"E145.sketch_text.stroke-269"),sQuery(id+"F10.wireOp",EDGE,"E145.sketch_text.stroke-270"),sQuery(id+"F10.wireOp",EDGE,"E145.sketch_text.stroke-271"),sQuery(id+"F10.wireOp",EDGE,"E145.sketch_text.stroke-272"),sQuery(id+"F10.wireOp",EDGE,"E145.sketch_text.stroke-273"),sQuery(id+"F10.wireOp",EDGE,"E145.sketch_text.stroke-274"),sQuery(id+"F10.wireOp",EDGE,"E145.sketch_text.stroke-275"),sQuery(id+"F10.wireOp",EDGE,"E145.sketch_text.stroke-276"),sQuery(id+"F10.wireOp",EDGE,"E145.sketch_text.stroke-277"),sQuery(id+"F10.wireOp",EDGE,"E145.sketch_text.stroke-278"),sQuery(id+"F10.wireOp",EDGE,"E145.sketch_text.stroke-279"),sQuery(id+"F10.wireOp",EDGE,"E145.sketch_text.stroke-280"),sQuery(id+"F10.wireOp",EDGE,"E145.sketch_text.stroke-281"),sQuery(id+"F10.wireOp",EDGE,"E145.sketch_text.stroke-282"),sQuery(id+"F10.wireOp",EDGE,"E145.sketch_text.stroke-283"),sQuery(id+"F10.wireOp",EDGE,"E145.sketch_text.stroke-284")])]});
            var Q17;
            Q17=makeQuery(id+"F11.opExtrude","SWEPT_BODY",BODY,{"disambiguationData":[OSD([sQuery(id+"F10.wireOp",EDGE,"E145.sketch_text.stroke-285"),sQuery(id+"F10.wireOp",EDGE,"E145.sketch_text.stroke-286"),sQuery(id+"F10.wireOp",EDGE,"E145.sketch_text.stroke-287"),sQuery(id+"F10.wireOp",EDGE,"E145.sketch_text.stroke-288"),sQuery(id+"F10.wireOp",EDGE,"E145.sketch_text.stroke-289"),sQuery(id+"F10.wireOp",EDGE,"E145.sketch_text.stroke-290"),sQuery(id+"F10.wireOp",EDGE,"E145.sketch_text.stroke-291"),sQuery(id+"F10.wireOp",EDGE,"E145.sketch_text.stroke-292"),sQuery(id+"F10.wireOp",EDGE,"E145.sketch_text.stroke-293")])]});
            var Q18;
            Q18=makeQuery(id+"F11.opExtrude","SWEPT_BODY",BODY,{"disambiguationData":[OSD([sQuery(id+"F10.wireOp",EDGE,"E145.sketch_text.stroke-294"),sQuery(id+"F10.wireOp",EDGE,"E145.sketch_text.stroke-295"),sQuery(id+"F10.wireOp",EDGE,"E145.sketch_text.stroke-296"),sQuery(id+"F10.wireOp",EDGE,"E145.sketch_text.stroke-297"),sQuery(id+"F10.wireOp",EDGE,"E145.sketch_text.stroke-298"),sQuery(id+"F10.wireOp",EDGE,"E145.sketch_text.stroke-299"),sQuery(id+"F10.wireOp",EDGE,"E145.sketch_text.stroke-300"),sQuery(id+"F10.wireOp",EDGE,"E145.sketch_text.stroke-301"),sQuery(id+"F10.wireOp",EDGE,"E145.sketch_text.stroke-302"),sQuery(id+"F10.wireOp",EDGE,"E145.sketch_text.stroke-303"),sQuery(id+"F10.wireOp",EDGE,"E145.sketch_text.stroke-304"),sQuery(id+"F10.wireOp",EDGE,"E145.sketch_text.stroke-305"),sQuery(id+"F10.wireOp",EDGE,"E145.sketch_text.stroke-306"),sQuery(id+"F10.wireOp",EDGE,"E145.sketch_text.stroke-307"),sQuery(id+"F10.wireOp",EDGE,"E145.sketch_text.stroke-308"),sQuery(id+"F10.wireOp",EDGE,"E145.sketch_text.stroke-309"),sQuery(id+"F10.wireOp",EDGE,"E145.sketch_text.stroke-310"),sQuery(id+"F10.wireOp",EDGE,"E145.sketch_text.stroke-311"),sQuery(id+"F10.wireOp",EDGE,"E145.sketch_text.stroke-312"),sQuery(id+"F10.wireOp",EDGE,"E145.sketch_text.stroke-313"),sQuery(id+"F10.wireOp",EDGE,"E145.sketch_text.stroke-314"),sQuery(id+"F10.wireOp",EDGE,"E145.sketch_text.stroke-315"),sQuery(id+"F10.wireOp",EDGE,"E145.sketch_text.stroke-316"),sQuery(id+"F10.wireOp",EDGE,"E145.sketch_text.stroke-317"),sQuery(id+"F10.wireOp",EDGE,"E145.sketch_text.stroke-318")])]});
            var Q19;
            Q19=qCreatedBy(makeId("Origin.pointOp"),VERTEX);
            transform(context, id + "F12", {"entities" : qUnion([Q0, Q1, Q2, Q3, Q4, Q5, Q6, Q7, Q8, Q9, Q10, Q11, Q12, Q13, Q14, Q15, Q16, Q17, Q18]), "transformType" : TransformType.SCALE_UNIFORMLY, "scale" : .35, "scalePoint" : qUnion([Q19]), "makeCopy" : false});
        }
        {
            var Q0;
            Q0=makeQuery(id+"F11.opExtrude","SWEPT_BODY",BODY,{"disambiguationData":[OSD([sQuery(id+"F10.wireOp",EDGE,"E145.sketch_text.stroke-0"),sQuery(id+"F10.wireOp",EDGE,"E145.sketch_text.stroke-1"),sQuery(id+"F10.wireOp",EDGE,"E145.sketch_text.stroke-2"),sQuery(id+"F10.wireOp",EDGE,"E145.sketch_text.stroke-3"),sQuery(id+"F10.wireOp",EDGE,"E145.sketch_text.stroke-4"),sQuery(id+"F10.wireOp",EDGE,"E145.sketch_text.stroke-5"),sQuery(id+"F10.wireOp",EDGE,"E145.sketch_text.stroke-6"),sQuery(id+"F10.wireOp",EDGE,"E145.sketch_text.stroke-7"),sQuery(id+"F10.wireOp",EDGE,"E145.sketch_text.stroke-8"),sQuery(id+"F10.wireOp",EDGE,"E145.sketch_text.stroke-9"),sQuery(id+"F10.wireOp",EDGE,"E145.sketch_text.stroke-10"),sQuery(id+"F10.wireOp",EDGE,"E145.sketch_text.stroke-11"),sQuery(id+"F10.wireOp",EDGE,"E145.sketch_text.stroke-12")])]});
            var Q1;
            Q1=makeQuery(id+"F11.opExtrude","SWEPT_BODY",BODY,{"disambiguationData":[OSD([sQuery(id+"F10.wireOp",EDGE,"E145.sketch_text.stroke-26"),sQuery(id+"F10.wireOp",EDGE,"E145.sketch_text.stroke-27"),sQuery(id+"F10.wireOp",EDGE,"E145.sketch_text.stroke-28"),sQuery(id+"F10.wireOp",EDGE,"E145.sketch_text.stroke-29"),sQuery(id+"F10.wireOp",EDGE,"E145.sketch_text.stroke-30"),sQuery(id+"F10.wireOp",EDGE,"E145.sketch_text.stroke-31"),sQuery(id+"F10.wireOp",EDGE,"E145.sketch_text.stroke-32"),sQuery(id+"F10.wireOp",EDGE,"E145.sketch_text.stroke-33"),sQuery(id+"F10.wireOp",EDGE,"E145.sketch_text.stroke-34"),sQuery(id+"F10.wireOp",EDGE,"E145.sketch_text.stroke-35"),sQuery(id+"F10.wireOp",EDGE,"E145.sketch_text.stroke-36"),sQuery(id+"F10.wireOp",EDGE,"E145.sketch_text.stroke-37"),sQuery(id+"F10.wireOp",EDGE,"E145.sketch_text.stroke-38"),sQuery(id+"F10.wireOp",EDGE,"E145.sketch_text.stroke-39"),sQuery(id+"F10.wireOp",EDGE,"E145.sketch_text.stroke-40"),sQuery(id+"F10.wireOp",EDGE,"E145.sketch_text.stroke-41"),sQuery(id+"F10.wireOp",EDGE,"E145.sketch_text.stroke-42"),sQuery(id+"F10.wireOp",EDGE,"E145.sketch_text.stroke-43"),sQuery(id+"F10.wireOp",EDGE,"E145.sketch_text.stroke-44"),sQuery(id+"F10.wireOp",EDGE,"E145.sketch_text.stroke-45"),sQuery(id+"F10.wireOp",EDGE,"E145.sketch_text.stroke-46"),sQuery(id+"F10.wireOp",EDGE,"E145.sketch_text.stroke-47"),sQuery(id+"F10.wireOp",EDGE,"E145.sketch_text.stroke-48"),sQuery(id+"F10.wireOp",EDGE,"E145.sketch_text.stroke-49")])]});
            var Q2;
            Q2=makeQuery(id+"F11.opExtrude","SWEPT_BODY",BODY,{"disambiguationData":[OSD([sQuery(id+"F10.wireOp",EDGE,"E145.sketch_text.stroke-13"),sQuery(id+"F10.wireOp",EDGE,"E145.sketch_text.stroke-14"),sQuery(id+"F10.wireOp",EDGE,"E145.sketch_text.stroke-15"),sQuery(id+"F10.wireOp",EDGE,"E145.sketch_text.stroke-16"),sQuery(id+"F10.wireOp",EDGE,"E145.sketch_text.stroke-17"),sQuery(id+"F10.wireOp",EDGE,"E145.sketch_text.stroke-18"),sQuery(id+"F10.wireOp",EDGE,"E145.sketch_text.stroke-19"),sQuery(id+"F10.wireOp",EDGE,"E145.sketch_text.stroke-20"),sQuery(id+"F10.wireOp",EDGE,"E145.sketch_text.stroke-21"),sQuery(id+"F10.wireOp",EDGE,"E145.sketch_text.stroke-22"),sQuery(id+"F10.wireOp",EDGE,"E145.sketch_text.stroke-23"),sQuery(id+"F10.wireOp",EDGE,"E145.sketch_text.stroke-24"),sQuery(id+"F10.wireOp",EDGE,"E145.sketch_text.stroke-25")])]});
            var Q3;
            Q3=makeQuery(id+"F11.opExtrude","SWEPT_BODY",BODY,{"disambiguationData":[OSD([sQuery(id+"F10.wireOp",EDGE,"E145.sketch_text.stroke-50"),sQuery(id+"F10.wireOp",EDGE,"E145.sketch_text.stroke-51"),sQuery(id+"F10.wireOp",EDGE,"E145.sketch_text.stroke-52"),sQuery(id+"F10.wireOp",EDGE,"E145.sketch_text.stroke-53"),sQuery(id+"F10.wireOp",EDGE,"E145.sketch_text.stroke-54"),sQuery(id+"F10.wireOp",EDGE,"E145.sketch_text.stroke-55"),sQuery(id+"F10.wireOp",EDGE,"E145.sketch_text.stroke-56"),sQuery(id+"F10.wireOp",EDGE,"E145.sketch_text.stroke-57"),sQuery(id+"F10.wireOp",EDGE,"E145.sketch_text.stroke-58"),sQuery(id+"F10.wireOp",EDGE,"E145.sketch_text.stroke-59"),sQuery(id+"F10.wireOp",EDGE,"E145.sketch_text.stroke-60"),sQuery(id+"F10.wireOp",EDGE,"E145.sketch_text.stroke-61"),sQuery(id+"F10.wireOp",EDGE,"E145.sketch_text.stroke-62"),sQuery(id+"F10.wireOp",EDGE,"E145.sketch_text.stroke-63"),sQuery(id+"F10.wireOp",EDGE,"E145.sketch_text.stroke-64"),sQuery(id+"F10.wireOp",EDGE,"E145.sketch_text.stroke-65"),sQuery(id+"F10.wireOp",EDGE,"E145.sketch_text.stroke-66"),sQuery(id+"F10.wireOp",EDGE,"E145.sketch_text.stroke-67"),sQuery(id+"F10.wireOp",EDGE,"E145.sketch_text.stroke-68")])]});
            var Q4;
            Q4=makeQuery(id+"F11.opExtrude","SWEPT_BODY",BODY,{"disambiguationData":[OSD([sQuery(id+"F10.wireOp",EDGE,"E145.sketch_text.stroke-86"),sQuery(id+"F10.wireOp",EDGE,"E145.sketch_text.stroke-87"),sQuery(id+"F10.wireOp",EDGE,"E145.sketch_text.stroke-88"),sQuery(id+"F10.wireOp",EDGE,"E145.sketch_text.stroke-89"),sQuery(id+"F10.wireOp",EDGE,"E145.sketch_text.stroke-90"),sQuery(id+"F10.wireOp",EDGE,"E145.sketch_text.stroke-91"),sQuery(id+"F10.wireOp",EDGE,"E145.sketch_text.stroke-92"),sQuery(id+"F10.wireOp",EDGE,"E145.sketch_text.stroke-93")])]});
            var Q5;
            Q5=makeQuery(id+"F11.opExtrude","SWEPT_BODY",BODY,{"disambiguationData":[OSD([sQuery(id+"F10.wireOp",EDGE,"E145.sketch_text.stroke-69"),sQuery(id+"F10.wireOp",EDGE,"E145.sketch_text.stroke-70"),sQuery(id+"F10.wireOp",EDGE,"E145.sketch_text.stroke-71"),sQuery(id+"F10.wireOp",EDGE,"E145.sketch_text.stroke-72"),sQuery(id+"F10.wireOp",EDGE,"E145.sketch_text.stroke-73"),sQuery(id+"F10.wireOp",EDGE,"E145.sketch_text.stroke-74"),sQuery(id+"F10.wireOp",EDGE,"E145.sketch_text.stroke-75"),sQuery(id+"F10.wireOp",EDGE,"E145.sketch_text.stroke-76"),sQuery(id+"F10.wireOp",EDGE,"E145.sketch_text.stroke-77"),sQuery(id+"F10.wireOp",EDGE,"E145.sketch_text.stroke-78"),sQuery(id+"F10.wireOp",EDGE,"E145.sketch_text.stroke-79"),sQuery(id+"F10.wireOp",EDGE,"E145.sketch_text.stroke-80"),sQuery(id+"F10.wireOp",EDGE,"E145.sketch_text.stroke-81"),sQuery(id+"F10.wireOp",EDGE,"E145.sketch_text.stroke-82"),sQuery(id+"F10.wireOp",EDGE,"E145.sketch_text.stroke-83"),sQuery(id+"F10.wireOp",EDGE,"E145.sketch_text.stroke-84"),sQuery(id+"F10.wireOp",EDGE,"E145.sketch_text.stroke-85")])]});
            var Q6;
            Q6=makeQuery(id+"F11.opExtrude","SWEPT_BODY",BODY,{"disambiguationData":[OSD([sQuery(id+"F10.wireOp",EDGE,"E145.sketch_text.stroke-94"),sQuery(id+"F10.wireOp",EDGE,"E145.sketch_text.stroke-95"),sQuery(id+"F10.wireOp",EDGE,"E145.sketch_text.stroke-96"),sQuery(id+"F10.wireOp",EDGE,"E145.sketch_text.stroke-97"),sQuery(id+"F10.wireOp",EDGE,"E145.sketch_text.stroke-98"),sQuery(id+"F10.wireOp",EDGE,"E145.sketch_text.stroke-99"),sQuery(id+"F10.wireOp",EDGE,"E145.sketch_text.stroke-100"),sQuery(id+"F10.wireOp",EDGE,"E145.sketch_text.stroke-101"),sQuery(id+"F10.wireOp",EDGE,"E145.sketch_text.stroke-102"),sQuery(id+"F10.wireOp",EDGE,"E145.sketch_text.stroke-103"),sQuery(id+"F10.wireOp",EDGE,"E145.sketch_text.stroke-104"),sQuery(id+"F10.wireOp",EDGE,"E145.sketch_text.stroke-105"),sQuery(id+"F10.wireOp",EDGE,"E145.sketch_text.stroke-106"),sQuery(id+"F10.wireOp",EDGE,"E145.sketch_text.stroke-107"),sQuery(id+"F10.wireOp",EDGE,"E145.sketch_text.stroke-108"),sQuery(id+"F10.wireOp",EDGE,"E145.sketch_text.stroke-109"),sQuery(id+"F10.wireOp",EDGE,"E145.sketch_text.stroke-110"),sQuery(id+"F10.wireOp",EDGE,"E145.sketch_text.stroke-111")])]});
            var Q7;
            Q7=makeQuery(id+"F11.opExtrude","SWEPT_BODY",BODY,{"disambiguationData":[OSD([sQuery(id+"F10.wireOp",EDGE,"E145.sketch_text.stroke-112"),sQuery(id+"F10.wireOp",EDGE,"E145.sketch_text.stroke-113"),sQuery(id+"F10.wireOp",EDGE,"E145.sketch_text.stroke-114"),sQuery(id+"F10.wireOp",EDGE,"E145.sketch_text.stroke-115"),sQuery(id+"F10.wireOp",EDGE,"E145.sketch_text.stroke-116"),sQuery(id+"F10.wireOp",EDGE,"E145.sketch_text.stroke-117"),sQuery(id+"F10.wireOp",EDGE,"E145.sketch_text.stroke-118"),sQuery(id+"F10.wireOp",EDGE,"E145.sketch_text.stroke-119"),sQuery(id+"F10.wireOp",EDGE,"E145.sketch_text.stroke-120"),sQuery(id+"F10.wireOp",EDGE,"E145.sketch_text.stroke-121"),sQuery(id+"F10.wireOp",EDGE,"E145.sketch_text.stroke-122"),sQuery(id+"F10.wireOp",EDGE,"E145.sketch_text.stroke-123"),sQuery(id+"F10.wireOp",EDGE,"E145.sketch_text.stroke-124"),sQuery(id+"F10.wireOp",EDGE,"E145.sketch_text.stroke-125"),sQuery(id+"F10.wireOp",EDGE,"E145.sketch_text.stroke-126"),sQuery(id+"F10.wireOp",EDGE,"E145.sketch_text.stroke-127"),sQuery(id+"F10.wireOp",EDGE,"E145.sketch_text.stroke-128"),sQuery(id+"F10.wireOp",EDGE,"E145.sketch_text.stroke-129"),sQuery(id+"F10.wireOp",EDGE,"E145.sketch_text.stroke-130")])]});
            var Q8;
            Q8=makeQuery(id+"F11.opExtrude","SWEPT_BODY",BODY,{"disambiguationData":[OSD([sQuery(id+"F10.wireOp",EDGE,"E145.sketch_text.stroke-131"),sQuery(id+"F10.wireOp",EDGE,"E145.sketch_text.stroke-132"),sQuery(id+"F10.wireOp",EDGE,"E145.sketch_text.stroke-133"),sQuery(id+"F10.wireOp",EDGE,"E145.sketch_text.stroke-134"),sQuery(id+"F10.wireOp",EDGE,"E145.sketch_text.stroke-135"),sQuery(id+"F10.wireOp",EDGE,"E145.sketch_text.stroke-136"),sQuery(id+"F10.wireOp",EDGE,"E145.sketch_text.stroke-137"),sQuery(id+"F10.wireOp",EDGE,"E145.sketch_text.stroke-138"),sQuery(id+"F10.wireOp",EDGE,"E145.sketch_text.stroke-139"),sQuery(id+"F10.wireOp",EDGE,"E145.sketch_text.stroke-140"),sQuery(id+"F10.wireOp",EDGE,"E145.sketch_text.stroke-141"),sQuery(id+"F10.wireOp",EDGE,"E145.sketch_text.stroke-142"),sQuery(id+"F10.wireOp",EDGE,"E145.sketch_text.stroke-143"),sQuery(id+"F10.wireOp",EDGE,"E145.sketch_text.stroke-144"),sQuery(id+"F10.wireOp",EDGE,"E145.sketch_text.stroke-145"),sQuery(id+"F10.wireOp",EDGE,"E145.sketch_text.stroke-146"),sQuery(id+"F10.wireOp",EDGE,"E145.sketch_text.stroke-147"),sQuery(id+"F10.wireOp",EDGE,"E145.sketch_text.stroke-148"),sQuery(id+"F10.wireOp",EDGE,"E145.sketch_text.stroke-149"),sQuery(id+"F10.wireOp",EDGE,"E145.sketch_text.stroke-150"),sQuery(id+"F10.wireOp",EDGE,"E145.sketch_text.stroke-151"),sQuery(id+"F10.wireOp",EDGE,"E145.sketch_text.stroke-152"),sQuery(id+"F10.wireOp",EDGE,"E145.sketch_text.stroke-153"),sQuery(id+"F10.wireOp",EDGE,"E145.sketch_text.stroke-154"),sQuery(id+"F10.wireOp",EDGE,"E145.sketch_text.stroke-155"),sQuery(id+"F10.wireOp",EDGE,"E145.sketch_text.stroke-156"),sQuery(id+"F10.wireOp",EDGE,"E145.sketch_text.stroke-157")])]});
            var Q9;
            Q9=makeQuery(id+"F11.opExtrude","SWEPT_BODY",BODY,{"disambiguationData":[OSD([sQuery(id+"F10.wireOp",EDGE,"E145.sketch_text.stroke-190"),sQuery(id+"F10.wireOp",EDGE,"E145.sketch_text.stroke-191"),sQuery(id+"F10.wireOp",EDGE,"E145.sketch_text.stroke-192"),sQuery(id+"F10.wireOp",EDGE,"E145.sketch_text.stroke-193"),sQuery(id+"F10.wireOp",EDGE,"E145.sketch_text.stroke-194"),sQuery(id+"F10.wireOp",EDGE,"E145.sketch_text.stroke-195"),sQuery(id+"F10.wireOp",EDGE,"E145.sketch_text.stroke-196"),sQuery(id+"F10.wireOp",EDGE,"E145.sketch_text.stroke-197"),sQuery(id+"F10.wireOp",EDGE,"E145.sketch_text.stroke-198"),sQuery(id+"F10.wireOp",EDGE,"E145.sketch_text.stroke-199"),sQuery(id+"F10.wireOp",EDGE,"E145.sketch_text.stroke-200"),sQuery(id+"F10.wireOp",EDGE,"E145.sketch_text.stroke-201"),sQuery(id+"F10.wireOp",EDGE,"E145.sketch_text.stroke-202"),sQuery(id+"F10.wireOp",EDGE,"E145.sketch_text.stroke-203"),sQuery(id+"F10.wireOp",EDGE,"E145.sketch_text.stroke-204"),sQuery(id+"F10.wireOp",EDGE,"E145.sketch_text.stroke-205"),sQuery(id+"F10.wireOp",EDGE,"E145.sketch_text.stroke-206"),sQuery(id+"F10.wireOp",EDGE,"E145.sketch_text.stroke-207"),sQuery(id+"F10.wireOp",EDGE,"E145.sketch_text.stroke-208")])]});
            var Q10;
            Q10=makeQuery(id+"F11.opExtrude","SWEPT_BODY",BODY,{"disambiguationData":[OSD([sQuery(id+"F10.wireOp",EDGE,"E145.sketch_text.stroke-158"),sQuery(id+"F10.wireOp",EDGE,"E145.sketch_text.stroke-159"),sQuery(id+"F10.wireOp",EDGE,"E145.sketch_text.stroke-160"),sQuery(id+"F10.wireOp",EDGE,"E145.sketch_text.stroke-161"),sQuery(id+"F10.wireOp",EDGE,"E145.sketch_text.stroke-162"),sQuery(id+"F10.wireOp",EDGE,"E145.sketch_text.stroke-163"),sQuery(id+"F10.wireOp",EDGE,"E145.sketch_text.stroke-164"),sQuery(id+"F10.wireOp",EDGE,"E145.sketch_text.stroke-165"),sQuery(id+"F10.wireOp",EDGE,"E145.sketch_text.stroke-166"),sQuery(id+"F10.wireOp",EDGE,"E145.sketch_text.stroke-167"),sQuery(id+"F10.wireOp",EDGE,"E145.sketch_text.stroke-168"),sQuery(id+"F10.wireOp",EDGE,"E145.sketch_text.stroke-169"),sQuery(id+"F10.wireOp",EDGE,"E145.sketch_text.stroke-170"),sQuery(id+"F10.wireOp",EDGE,"E145.sketch_text.stroke-171"),sQuery(id+"F10.wireOp",EDGE,"E145.sketch_text.stroke-172"),sQuery(id+"F10.wireOp",EDGE,"E145.sketch_text.stroke-173"),sQuery(id+"F10.wireOp",EDGE,"E145.sketch_text.stroke-174"),sQuery(id+"F10.wireOp",EDGE,"E145.sketch_text.stroke-175"),sQuery(id+"F10.wireOp",EDGE,"E145.sketch_text.stroke-176")])]});
            var Q11;
            Q11=makeQuery(id+"F11.opExtrude","SWEPT_BODY",BODY,{"disambiguationData":[OSD([sQuery(id+"F10.wireOp",EDGE,"E145.sketch_text.stroke-177"),sQuery(id+"F10.wireOp",EDGE,"E145.sketch_text.stroke-178"),sQuery(id+"F10.wireOp",EDGE,"E145.sketch_text.stroke-179"),sQuery(id+"F10.wireOp",EDGE,"E145.sketch_text.stroke-180"),sQuery(id+"F10.wireOp",EDGE,"E145.sketch_text.stroke-181"),sQuery(id+"F10.wireOp",EDGE,"E145.sketch_text.stroke-182"),sQuery(id+"F10.wireOp",EDGE,"E145.sketch_text.stroke-183"),sQuery(id+"F10.wireOp",EDGE,"E145.sketch_text.stroke-184"),sQuery(id+"F10.wireOp",EDGE,"E145.sketch_text.stroke-185"),sQuery(id+"F10.wireOp",EDGE,"E145.sketch_text.stroke-186"),sQuery(id+"F10.wireOp",EDGE,"E145.sketch_text.stroke-187"),sQuery(id+"F10.wireOp",EDGE,"E145.sketch_text.stroke-188"),sQuery(id+"F10.wireOp",EDGE,"E145.sketch_text.stroke-189")])]});
            var Q12;
            Q12=makeQuery(id+"F11.opExtrude","SWEPT_BODY",BODY,{"disambiguationData":[OSD([sQuery(id+"F10.wireOp",EDGE,"E145.sketch_text.stroke-224"),sQuery(id+"F10.wireOp",EDGE,"E145.sketch_text.stroke-225"),sQuery(id+"F10.wireOp",EDGE,"E145.sketch_text.stroke-226"),sQuery(id+"F10.wireOp",EDGE,"E145.sketch_text.stroke-227"),sQuery(id+"F10.wireOp",EDGE,"E145.sketch_text.stroke-228"),sQuery(id+"F10.wireOp",EDGE,"E145.sketch_text.stroke-229"),sQuery(id+"F10.wireOp",EDGE,"E145.sketch_text.stroke-230"),sQuery(id+"F10.wireOp",EDGE,"E145.sketch_text.stroke-231"),sQuery(id+"F10.wireOp",EDGE,"E145.sketch_text.stroke-232"),sQuery(id+"F10.wireOp",EDGE,"E145.sketch_text.stroke-233"),sQuery(id+"F10.wireOp",EDGE,"E145.sketch_text.stroke-234"),sQuery(id+"F10.wireOp",EDGE,"E145.sketch_text.stroke-235"),sQuery(id+"F10.wireOp",EDGE,"E145.sketch_text.stroke-236"),sQuery(id+"F10.wireOp",EDGE,"E145.sketch_text.stroke-237"),sQuery(id+"F10.wireOp",EDGE,"E145.sketch_text.stroke-238"),sQuery(id+"F10.wireOp",EDGE,"E145.sketch_text.stroke-239"),sQuery(id+"F10.wireOp",EDGE,"E145.sketch_text.stroke-240")])]});
            var Q13;
            Q13=makeQuery(id+"F11.opExtrude","SWEPT_BODY",BODY,{"disambiguationData":[OSD([sQuery(id+"F10.wireOp",EDGE,"E145.sketch_text.stroke-209"),sQuery(id+"F10.wireOp",EDGE,"E145.sketch_text.stroke-210"),sQuery(id+"F10.wireOp",EDGE,"E145.sketch_text.stroke-211"),sQuery(id+"F10.wireOp",EDGE,"E145.sketch_text.stroke-212"),sQuery(id+"F10.wireOp",EDGE,"E145.sketch_text.stroke-213"),sQuery(id+"F10.wireOp",EDGE,"E145.sketch_text.stroke-214"),sQuery(id+"F10.wireOp",EDGE,"E145.sketch_text.stroke-215"),sQuery(id+"F10.wireOp",EDGE,"E145.sketch_text.stroke-216"),sQuery(id+"F10.wireOp",EDGE,"E145.sketch_text.stroke-217"),sQuery(id+"F10.wireOp",EDGE,"E145.sketch_text.stroke-218"),sQuery(id+"F10.wireOp",EDGE,"E145.sketch_text.stroke-219"),sQuery(id+"F10.wireOp",EDGE,"E145.sketch_text.stroke-220"),sQuery(id+"F10.wireOp",EDGE,"E145.sketch_text.stroke-221"),sQuery(id+"F10.wireOp",EDGE,"E145.sketch_text.stroke-222"),sQuery(id+"F10.wireOp",EDGE,"E145.sketch_text.stroke-223")])]});
            var Q14;
            Q14=makeQuery(id+"F11.opExtrude","SWEPT_BODY",BODY,{"disambiguationData":[OSD([sQuery(id+"F10.wireOp",EDGE,"E145.sketch_text.stroke-249"),sQuery(id+"F10.wireOp",EDGE,"E145.sketch_text.stroke-250"),sQuery(id+"F10.wireOp",EDGE,"E145.sketch_text.stroke-251"),sQuery(id+"F10.wireOp",EDGE,"E145.sketch_text.stroke-252"),sQuery(id+"F10.wireOp",EDGE,"E145.sketch_text.stroke-253"),sQuery(id+"F10.wireOp",EDGE,"E145.sketch_text.stroke-254"),sQuery(id+"F10.wireOp",EDGE,"E145.sketch_text.stroke-255"),sQuery(id+"F10.wireOp",EDGE,"E145.sketch_text.stroke-256"),sQuery(id+"F10.wireOp",EDGE,"E145.sketch_text.stroke-257"),sQuery(id+"F10.wireOp",EDGE,"E145.sketch_text.stroke-258"),sQuery(id+"F10.wireOp",EDGE,"E145.sketch_text.stroke-259"),sQuery(id+"F10.wireOp",EDGE,"E145.sketch_text.stroke-260"),sQuery(id+"F10.wireOp",EDGE,"E145.sketch_text.stroke-261"),sQuery(id+"F10.wireOp",EDGE,"E145.sketch_text.stroke-262"),sQuery(id+"F10.wireOp",EDGE,"E145.sketch_text.stroke-263"),sQuery(id+"F10.wireOp",EDGE,"E145.sketch_text.stroke-264"),sQuery(id+"F10.wireOp",EDGE,"E145.sketch_text.stroke-265"),sQuery(id+"F10.wireOp",EDGE,"E145.sketch_text.stroke-266"),sQuery(id+"F10.wireOp",EDGE,"E145.sketch_text.stroke-267"),sQuery(id+"F10.wireOp",EDGE,"E145.sketch_text.stroke-268")])]});
            var Q15;
            Q15=makeQuery(id+"F11.opExtrude","SWEPT_BODY",BODY,{"disambiguationData":[OSD([sQuery(id+"F10.wireOp",EDGE,"E145.sketch_text.stroke-241"),sQuery(id+"F10.wireOp",EDGE,"E145.sketch_text.stroke-242"),sQuery(id+"F10.wireOp",EDGE,"E145.sketch_text.stroke-243"),sQuery(id+"F10.wireOp",EDGE,"E145.sketch_text.stroke-244"),sQuery(id+"F10.wireOp",EDGE,"E145.sketch_text.stroke-245"),sQuery(id+"F10.wireOp",EDGE,"E145.sketch_text.stroke-246"),sQuery(id+"F10.wireOp",EDGE,"E145.sketch_text.stroke-247"),sQuery(id+"F10.wireOp",EDGE,"E145.sketch_text.stroke-248")])]});
            var Q16;
            Q16=makeQuery(id+"F11.opExtrude","SWEPT_BODY",BODY,{"disambiguationData":[OSD([sQuery(id+"F10.wireOp",EDGE,"E145.sketch_text.stroke-269"),sQuery(id+"F10.wireOp",EDGE,"E145.sketch_text.stroke-270"),sQuery(id+"F10.wireOp",EDGE,"E145.sketch_text.stroke-271"),sQuery(id+"F10.wireOp",EDGE,"E145.sketch_text.stroke-272"),sQuery(id+"F10.wireOp",EDGE,"E145.sketch_text.stroke-273"),sQuery(id+"F10.wireOp",EDGE,"E145.sketch_text.stroke-274"),sQuery(id+"F10.wireOp",EDGE,"E145.sketch_text.stroke-275"),sQuery(id+"F10.wireOp",EDGE,"E145.sketch_text.stroke-276"),sQuery(id+"F10.wireOp",EDGE,"E145.sketch_text.stroke-277"),sQuery(id+"F10.wireOp",EDGE,"E145.sketch_text.stroke-278"),sQuery(id+"F10.wireOp",EDGE,"E145.sketch_text.stroke-279"),sQuery(id+"F10.wireOp",EDGE,"E145.sketch_text.stroke-280"),sQuery(id+"F10.wireOp",EDGE,"E145.sketch_text.stroke-281"),sQuery(id+"F10.wireOp",EDGE,"E145.sketch_text.stroke-282"),sQuery(id+"F10.wireOp",EDGE,"E145.sketch_text.stroke-283"),sQuery(id+"F10.wireOp",EDGE,"E145.sketch_text.stroke-284")])]});
            var Q17;
            Q17=makeQuery(id+"F11.opExtrude","SWEPT_BODY",BODY,{"disambiguationData":[OSD([sQuery(id+"F10.wireOp",EDGE,"E145.sketch_text.stroke-285"),sQuery(id+"F10.wireOp",EDGE,"E145.sketch_text.stroke-286"),sQuery(id+"F10.wireOp",EDGE,"E145.sketch_text.stroke-287"),sQuery(id+"F10.wireOp",EDGE,"E145.sketch_text.stroke-288"),sQuery(id+"F10.wireOp",EDGE,"E145.sketch_text.stroke-289"),sQuery(id+"F10.wireOp",EDGE,"E145.sketch_text.stroke-290"),sQuery(id+"F10.wireOp",EDGE,"E145.sketch_text.stroke-291"),sQuery(id+"F10.wireOp",EDGE,"E145.sketch_text.stroke-292"),sQuery(id+"F10.wireOp",EDGE,"E145.sketch_text.stroke-293")])]});
            var Q18;
            Q18=makeQuery(id+"F11.opExtrude","SWEPT_BODY",BODY,{"disambiguationData":[OSD([sQuery(id+"F10.wireOp",EDGE,"E145.sketch_text.stroke-294"),sQuery(id+"F10.wireOp",EDGE,"E145.sketch_text.stroke-295"),sQuery(id+"F10.wireOp",EDGE,"E145.sketch_text.stroke-296"),sQuery(id+"F10.wireOp",EDGE,"E145.sketch_text.stroke-297"),sQuery(id+"F10.wireOp",EDGE,"E145.sketch_text.stroke-298"),sQuery(id+"F10.wireOp",EDGE,"E145.sketch_text.stroke-299"),sQuery(id+"F10.wireOp",EDGE,"E145.sketch_text.stroke-300"),sQuery(id+"F10.wireOp",EDGE,"E145.sketch_text.stroke-301"),sQuery(id+"F10.wireOp",EDGE,"E145.sketch_text.stroke-302"),sQuery(id+"F10.wireOp",EDGE,"E145.sketch_text.stroke-303"),sQuery(id+"F10.wireOp",EDGE,"E145.sketch_text.stroke-304"),sQuery(id+"F10.wireOp",EDGE,"E145.sketch_text.stroke-305"),sQuery(id+"F10.wireOp",EDGE,"E145.sketch_text.stroke-306"),sQuery(id+"F10.wireOp",EDGE,"E145.sketch_text.stroke-307"),sQuery(id+"F10.wireOp",EDGE,"E145.sketch_text.stroke-308"),sQuery(id+"F10.wireOp",EDGE,"E145.sketch_text.stroke-309"),sQuery(id+"F10.wireOp",EDGE,"E145.sketch_text.stroke-310"),sQuery(id+"F10.wireOp",EDGE,"E145.sketch_text.stroke-311"),sQuery(id+"F10.wireOp",EDGE,"E145.sketch_text.stroke-312"),sQuery(id+"F10.wireOp",EDGE,"E145.sketch_text.stroke-313"),sQuery(id+"F10.wireOp",EDGE,"E145.sketch_text.stroke-314"),sQuery(id+"F10.wireOp",EDGE,"E145.sketch_text.stroke-315"),sQuery(id+"F10.wireOp",EDGE,"E145.sketch_text.stroke-316"),sQuery(id+"F10.wireOp",EDGE,"E145.sketch_text.stroke-317"),sQuery(id+"F10.wireOp",EDGE,"E145.sketch_text.stroke-318")])]});
            transform(context, id + "F13", {"entities" : qUnion([Q0, Q1, Q2, Q3, Q4, Q5, Q6, Q7, Q8, Q9, Q10, Q11, Q12, Q13, Q14, Q15, Q16, Q17, Q18]), "transformType" : TransformType.TRANSLATION_3D, "dx" : -12.27 * mm, "dy" : -1.78 * mm, "dz" : 0 * mm, "makeCopy" : false});
        }
        {
            var Q0;
            Q0=makeQuery(id+"F11.opExtrude","CAP_FACE",FACE,{"disambiguationData":[OSD([sQuery(id+"F10.wireOp",EDGE,"E145.sketch_text.stroke-0"),sQuery(id+"F10.wireOp",EDGE,"E145.sketch_text.stroke-1"),sQuery(id+"F10.wireOp",EDGE,"E145.sketch_text.stroke-2"),sQuery(id+"F10.wireOp",EDGE,"E145.sketch_text.stroke-3"),sQuery(id+"F10.wireOp",EDGE,"E145.sketch_text.stroke-4"),sQuery(id+"F10.wireOp",EDGE,"E145.sketch_text.stroke-5"),sQuery(id+"F10.wireOp",EDGE,"E145.sketch_text.stroke-6"),sQuery(id+"F10.wireOp",EDGE,"E145.sketch_text.stroke-7"),sQuery(id+"F10.wireOp",EDGE,"E145.sketch_text.stroke-8"),sQuery(id+"F10.wireOp",EDGE,"E145.sketch_text.stroke-9"),sQuery(id+"F10.wireOp",EDGE,"E145.sketch_text.stroke-10"),sQuery(id+"F10.wireOp",EDGE,"E145.sketch_text.stroke-11"),sQuery(id+"F10.wireOp",EDGE,"E145.sketch_text.stroke-12")])],"isStart":false});
            var Q1;
            Q1=makeQuery(id+"F11.opExtrude","CAP_FACE",FACE,{"disambiguationData":[OSD([sQuery(id+"F10.wireOp",EDGE,"E145.sketch_text.stroke-13"),sQuery(id+"F10.wireOp",EDGE,"E145.sketch_text.stroke-14"),sQuery(id+"F10.wireOp",EDGE,"E145.sketch_text.stroke-15"),sQuery(id+"F10.wireOp",EDGE,"E145.sketch_text.stroke-16"),sQuery(id+"F10.wireOp",EDGE,"E145.sketch_text.stroke-17"),sQuery(id+"F10.wireOp",EDGE,"E145.sketch_text.stroke-18"),sQuery(id+"F10.wireOp",EDGE,"E145.sketch_text.stroke-19"),sQuery(id+"F10.wireOp",EDGE,"E145.sketch_text.stroke-20"),sQuery(id+"F10.wireOp",EDGE,"E145.sketch_text.stroke-21"),sQuery(id+"F10.wireOp",EDGE,"E145.sketch_text.stroke-22"),sQuery(id+"F10.wireOp",EDGE,"E145.sketch_text.stroke-23"),sQuery(id+"F10.wireOp",EDGE,"E145.sketch_text.stroke-24"),sQuery(id+"F10.wireOp",EDGE,"E145.sketch_text.stroke-25")])],"isStart":false});
            var Q2;
            Q2=makeQuery(id+"F11.opExtrude","CAP_FACE",FACE,{"disambiguationData":[OSD([sQuery(id+"F10.wireOp",EDGE,"E145.sketch_text.stroke-26"),sQuery(id+"F10.wireOp",EDGE,"E145.sketch_text.stroke-27"),sQuery(id+"F10.wireOp",EDGE,"E145.sketch_text.stroke-28"),sQuery(id+"F10.wireOp",EDGE,"E145.sketch_text.stroke-29"),sQuery(id+"F10.wireOp",EDGE,"E145.sketch_text.stroke-30"),sQuery(id+"F10.wireOp",EDGE,"E145.sketch_text.stroke-31"),sQuery(id+"F10.wireOp",EDGE,"E145.sketch_text.stroke-32"),sQuery(id+"F10.wireOp",EDGE,"E145.sketch_text.stroke-33"),sQuery(id+"F10.wireOp",EDGE,"E145.sketch_text.stroke-34"),sQuery(id+"F10.wireOp",EDGE,"E145.sketch_text.stroke-35"),sQuery(id+"F10.wireOp",EDGE,"E145.sketch_text.stroke-36"),sQuery(id+"F10.wireOp",EDGE,"E145.sketch_text.stroke-37"),sQuery(id+"F10.wireOp",EDGE,"E145.sketch_text.stroke-38"),sQuery(id+"F10.wireOp",EDGE,"E145.sketch_text.stroke-39"),sQuery(id+"F10.wireOp",EDGE,"E145.sketch_text.stroke-40"),sQuery(id+"F10.wireOp",EDGE,"E145.sketch_text.stroke-41"),sQuery(id+"F10.wireOp",EDGE,"E145.sketch_text.stroke-42"),sQuery(id+"F10.wireOp",EDGE,"E145.sketch_text.stroke-43"),sQuery(id+"F10.wireOp",EDGE,"E145.sketch_text.stroke-44"),sQuery(id+"F10.wireOp",EDGE,"E145.sketch_text.stroke-45"),sQuery(id+"F10.wireOp",EDGE,"E145.sketch_text.stroke-46"),sQuery(id+"F10.wireOp",EDGE,"E145.sketch_text.stroke-47"),sQuery(id+"F10.wireOp",EDGE,"E145.sketch_text.stroke-48"),sQuery(id+"F10.wireOp",EDGE,"E145.sketch_text.stroke-49")])],"isStart":false});
            var Q3;
            Q3=makeQuery(id+"F11.opExtrude","CAP_FACE",FACE,{"disambiguationData":[OSD([sQuery(id+"F10.wireOp",EDGE,"E145.sketch_text.stroke-50"),sQuery(id+"F10.wireOp",EDGE,"E145.sketch_text.stroke-51"),sQuery(id+"F10.wireOp",EDGE,"E145.sketch_text.stroke-52"),sQuery(id+"F10.wireOp",EDGE,"E145.sketch_text.stroke-53"),sQuery(id+"F10.wireOp",EDGE,"E145.sketch_text.stroke-54"),sQuery(id+"F10.wireOp",EDGE,"E145.sketch_text.stroke-55"),sQuery(id+"F10.wireOp",EDGE,"E145.sketch_text.stroke-56"),sQuery(id+"F10.wireOp",EDGE,"E145.sketch_text.stroke-57"),sQuery(id+"F10.wireOp",EDGE,"E145.sketch_text.stroke-58"),sQuery(id+"F10.wireOp",EDGE,"E145.sketch_text.stroke-59"),sQuery(id+"F10.wireOp",EDGE,"E145.sketch_text.stroke-60"),sQuery(id+"F10.wireOp",EDGE,"E145.sketch_text.stroke-61"),sQuery(id+"F10.wireOp",EDGE,"E145.sketch_text.stroke-62"),sQuery(id+"F10.wireOp",EDGE,"E145.sketch_text.stroke-63"),sQuery(id+"F10.wireOp",EDGE,"E145.sketch_text.stroke-64"),sQuery(id+"F10.wireOp",EDGE,"E145.sketch_text.stroke-65"),sQuery(id+"F10.wireOp",EDGE,"E145.sketch_text.stroke-66"),sQuery(id+"F10.wireOp",EDGE,"E145.sketch_text.stroke-67"),sQuery(id+"F10.wireOp",EDGE,"E145.sketch_text.stroke-68")])],"isStart":false});
            var Q4;
            Q4=makeQuery(id+"F11.opExtrude","CAP_FACE",FACE,{"disambiguationData":[OSD([sQuery(id+"F10.wireOp",EDGE,"E145.sketch_text.stroke-69"),sQuery(id+"F10.wireOp",EDGE,"E145.sketch_text.stroke-70"),sQuery(id+"F10.wireOp",EDGE,"E145.sketch_text.stroke-71"),sQuery(id+"F10.wireOp",EDGE,"E145.sketch_text.stroke-72"),sQuery(id+"F10.wireOp",EDGE,"E145.sketch_text.stroke-73"),sQuery(id+"F10.wireOp",EDGE,"E145.sketch_text.stroke-74"),sQuery(id+"F10.wireOp",EDGE,"E145.sketch_text.stroke-75"),sQuery(id+"F10.wireOp",EDGE,"E145.sketch_text.stroke-76"),sQuery(id+"F10.wireOp",EDGE,"E145.sketch_text.stroke-77"),sQuery(id+"F10.wireOp",EDGE,"E145.sketch_text.stroke-78"),sQuery(id+"F10.wireOp",EDGE,"E145.sketch_text.stroke-79"),sQuery(id+"F10.wireOp",EDGE,"E145.sketch_text.stroke-80"),sQuery(id+"F10.wireOp",EDGE,"E145.sketch_text.stroke-81"),sQuery(id+"F10.wireOp",EDGE,"E145.sketch_text.stroke-82"),sQuery(id+"F10.wireOp",EDGE,"E145.sketch_text.stroke-83"),sQuery(id+"F10.wireOp",EDGE,"E145.sketch_text.stroke-84"),sQuery(id+"F10.wireOp",EDGE,"E145.sketch_text.stroke-85")])],"isStart":false});
            var Q5;
            Q5=makeQuery(id+"F11.opExtrude","CAP_FACE",FACE,{"disambiguationData":[OSD([sQuery(id+"F10.wireOp",EDGE,"E145.sketch_text.stroke-86"),sQuery(id+"F10.wireOp",EDGE,"E145.sketch_text.stroke-87"),sQuery(id+"F10.wireOp",EDGE,"E145.sketch_text.stroke-88"),sQuery(id+"F10.wireOp",EDGE,"E145.sketch_text.stroke-89"),sQuery(id+"F10.wireOp",EDGE,"E145.sketch_text.stroke-90"),sQuery(id+"F10.wireOp",EDGE,"E145.sketch_text.stroke-91"),sQuery(id+"F10.wireOp",EDGE,"E145.sketch_text.stroke-92"),sQuery(id+"F10.wireOp",EDGE,"E145.sketch_text.stroke-93")])],"isStart":false});
            var Q6;
            Q6=makeQuery(id+"F11.opExtrude","CAP_FACE",FACE,{"disambiguationData":[OSD([sQuery(id+"F10.wireOp",EDGE,"E145.sketch_text.stroke-94"),sQuery(id+"F10.wireOp",EDGE,"E145.sketch_text.stroke-95"),sQuery(id+"F10.wireOp",EDGE,"E145.sketch_text.stroke-96"),sQuery(id+"F10.wireOp",EDGE,"E145.sketch_text.stroke-97"),sQuery(id+"F10.wireOp",EDGE,"E145.sketch_text.stroke-98"),sQuery(id+"F10.wireOp",EDGE,"E145.sketch_text.stroke-99"),sQuery(id+"F10.wireOp",EDGE,"E145.sketch_text.stroke-100"),sQuery(id+"F10.wireOp",EDGE,"E145.sketch_text.stroke-101"),sQuery(id+"F10.wireOp",EDGE,"E145.sketch_text.stroke-102"),sQuery(id+"F10.wireOp",EDGE,"E145.sketch_text.stroke-103"),sQuery(id+"F10.wireOp",EDGE,"E145.sketch_text.stroke-104"),sQuery(id+"F10.wireOp",EDGE,"E145.sketch_text.stroke-105"),sQuery(id+"F10.wireOp",EDGE,"E145.sketch_text.stroke-106"),sQuery(id+"F10.wireOp",EDGE,"E145.sketch_text.stroke-107"),sQuery(id+"F10.wireOp",EDGE,"E145.sketch_text.stroke-108"),sQuery(id+"F10.wireOp",EDGE,"E145.sketch_text.stroke-109"),sQuery(id+"F10.wireOp",EDGE,"E145.sketch_text.stroke-110"),sQuery(id+"F10.wireOp",EDGE,"E145.sketch_text.stroke-111")])],"isStart":false});
            var Q7;
            Q7=makeQuery(id+"F11.opExtrude","CAP_FACE",FACE,{"disambiguationData":[OSD([sQuery(id+"F10.wireOp",EDGE,"E145.sketch_text.stroke-112"),sQuery(id+"F10.wireOp",EDGE,"E145.sketch_text.stroke-113"),sQuery(id+"F10.wireOp",EDGE,"E145.sketch_text.stroke-114"),sQuery(id+"F10.wireOp",EDGE,"E145.sketch_text.stroke-115"),sQuery(id+"F10.wireOp",EDGE,"E145.sketch_text.stroke-116"),sQuery(id+"F10.wireOp",EDGE,"E145.sketch_text.stroke-117"),sQuery(id+"F10.wireOp",EDGE,"E145.sketch_text.stroke-118"),sQuery(id+"F10.wireOp",EDGE,"E145.sketch_text.stroke-119"),sQuery(id+"F10.wireOp",EDGE,"E145.sketch_text.stroke-120"),sQuery(id+"F10.wireOp",EDGE,"E145.sketch_text.stroke-121"),sQuery(id+"F10.wireOp",EDGE,"E145.sketch_text.stroke-122"),sQuery(id+"F10.wireOp",EDGE,"E145.sketch_text.stroke-123"),sQuery(id+"F10.wireOp",EDGE,"E145.sketch_text.stroke-124"),sQuery(id+"F10.wireOp",EDGE,"E145.sketch_text.stroke-125"),sQuery(id+"F10.wireOp",EDGE,"E145.sketch_text.stroke-126"),sQuery(id+"F10.wireOp",EDGE,"E145.sketch_text.stroke-127"),sQuery(id+"F10.wireOp",EDGE,"E145.sketch_text.stroke-128"),sQuery(id+"F10.wireOp",EDGE,"E145.sketch_text.stroke-129"),sQuery(id+"F10.wireOp",EDGE,"E145.sketch_text.stroke-130")])],"isStart":false});
            var Q8;
            Q8=makeQuery(id+"F11.opExtrude","CAP_FACE",FACE,{"disambiguationData":[OSD([sQuery(id+"F10.wireOp",EDGE,"E145.sketch_text.stroke-131"),sQuery(id+"F10.wireOp",EDGE,"E145.sketch_text.stroke-132"),sQuery(id+"F10.wireOp",EDGE,"E145.sketch_text.stroke-133"),sQuery(id+"F10.wireOp",EDGE,"E145.sketch_text.stroke-134"),sQuery(id+"F10.wireOp",EDGE,"E145.sketch_text.stroke-135"),sQuery(id+"F10.wireOp",EDGE,"E145.sketch_text.stroke-136"),sQuery(id+"F10.wireOp",EDGE,"E145.sketch_text.stroke-137"),sQuery(id+"F10.wireOp",EDGE,"E145.sketch_text.stroke-138"),sQuery(id+"F10.wireOp",EDGE,"E145.sketch_text.stroke-139"),sQuery(id+"F10.wireOp",EDGE,"E145.sketch_text.stroke-140"),sQuery(id+"F10.wireOp",EDGE,"E145.sketch_text.stroke-141"),sQuery(id+"F10.wireOp",EDGE,"E145.sketch_text.stroke-142"),sQuery(id+"F10.wireOp",EDGE,"E145.sketch_text.stroke-143"),sQuery(id+"F10.wireOp",EDGE,"E145.sketch_text.stroke-144"),sQuery(id+"F10.wireOp",EDGE,"E145.sketch_text.stroke-145"),sQuery(id+"F10.wireOp",EDGE,"E145.sketch_text.stroke-146"),sQuery(id+"F10.wireOp",EDGE,"E145.sketch_text.stroke-147"),sQuery(id+"F10.wireOp",EDGE,"E145.sketch_text.stroke-148"),sQuery(id+"F10.wireOp",EDGE,"E145.sketch_text.stroke-149"),sQuery(id+"F10.wireOp",EDGE,"E145.sketch_text.stroke-150"),sQuery(id+"F10.wireOp",EDGE,"E145.sketch_text.stroke-151"),sQuery(id+"F10.wireOp",EDGE,"E145.sketch_text.stroke-152"),sQuery(id+"F10.wireOp",EDGE,"E145.sketch_text.stroke-153"),sQuery(id+"F10.wireOp",EDGE,"E145.sketch_text.stroke-154"),sQuery(id+"F10.wireOp",EDGE,"E145.sketch_text.stroke-155"),sQuery(id+"F10.wireOp",EDGE,"E145.sketch_text.stroke-156"),sQuery(id+"F10.wireOp",EDGE,"E145.sketch_text.stroke-157")])],"isStart":false});
            var Q9;
            Q9=makeQuery(id+"F11.opExtrude","CAP_FACE",FACE,{"disambiguationData":[OSD([sQuery(id+"F10.wireOp",EDGE,"E145.sketch_text.stroke-158"),sQuery(id+"F10.wireOp",EDGE,"E145.sketch_text.stroke-159"),sQuery(id+"F10.wireOp",EDGE,"E145.sketch_text.stroke-160"),sQuery(id+"F10.wireOp",EDGE,"E145.sketch_text.stroke-161"),sQuery(id+"F10.wireOp",EDGE,"E145.sketch_text.stroke-162"),sQuery(id+"F10.wireOp",EDGE,"E145.sketch_text.stroke-163"),sQuery(id+"F10.wireOp",EDGE,"E145.sketch_text.stroke-164"),sQuery(id+"F10.wireOp",EDGE,"E145.sketch_text.stroke-165"),sQuery(id+"F10.wireOp",EDGE,"E145.sketch_text.stroke-166"),sQuery(id+"F10.wireOp",EDGE,"E145.sketch_text.stroke-167"),sQuery(id+"F10.wireOp",EDGE,"E145.sketch_text.stroke-168"),sQuery(id+"F10.wireOp",EDGE,"E145.sketch_text.stroke-169"),sQuery(id+"F10.wireOp",EDGE,"E145.sketch_text.stroke-170"),sQuery(id+"F10.wireOp",EDGE,"E145.sketch_text.stroke-171"),sQuery(id+"F10.wireOp",EDGE,"E145.sketch_text.stroke-172"),sQuery(id+"F10.wireOp",EDGE,"E145.sketch_text.stroke-173"),sQuery(id+"F10.wireOp",EDGE,"E145.sketch_text.stroke-174"),sQuery(id+"F10.wireOp",EDGE,"E145.sketch_text.stroke-175"),sQuery(id+"F10.wireOp",EDGE,"E145.sketch_text.stroke-176")])],"isStart":false});
            var Q10;
            Q10=makeQuery(id+"F11.opExtrude","CAP_FACE",FACE,{"disambiguationData":[OSD([sQuery(id+"F10.wireOp",EDGE,"E145.sketch_text.stroke-177"),sQuery(id+"F10.wireOp",EDGE,"E145.sketch_text.stroke-178"),sQuery(id+"F10.wireOp",EDGE,"E145.sketch_text.stroke-179"),sQuery(id+"F10.wireOp",EDGE,"E145.sketch_text.stroke-180"),sQuery(id+"F10.wireOp",EDGE,"E145.sketch_text.stroke-181"),sQuery(id+"F10.wireOp",EDGE,"E145.sketch_text.stroke-182"),sQuery(id+"F10.wireOp",EDGE,"E145.sketch_text.stroke-183"),sQuery(id+"F10.wireOp",EDGE,"E145.sketch_text.stroke-184"),sQuery(id+"F10.wireOp",EDGE,"E145.sketch_text.stroke-185"),sQuery(id+"F10.wireOp",EDGE,"E145.sketch_text.stroke-186"),sQuery(id+"F10.wireOp",EDGE,"E145.sketch_text.stroke-187"),sQuery(id+"F10.wireOp",EDGE,"E145.sketch_text.stroke-188"),sQuery(id+"F10.wireOp",EDGE,"E145.sketch_text.stroke-189")])],"isStart":false});
            var Q11;
            Q11=makeQuery(id+"F11.opExtrude","CAP_FACE",FACE,{"disambiguationData":[OSD([sQuery(id+"F10.wireOp",EDGE,"E145.sketch_text.stroke-294"),sQuery(id+"F10.wireOp",EDGE,"E145.sketch_text.stroke-295"),sQuery(id+"F10.wireOp",EDGE,"E145.sketch_text.stroke-296"),sQuery(id+"F10.wireOp",EDGE,"E145.sketch_text.stroke-297"),sQuery(id+"F10.wireOp",EDGE,"E145.sketch_text.stroke-298"),sQuery(id+"F10.wireOp",EDGE,"E145.sketch_text.stroke-299"),sQuery(id+"F10.wireOp",EDGE,"E145.sketch_text.stroke-300"),sQuery(id+"F10.wireOp",EDGE,"E145.sketch_text.stroke-301"),sQuery(id+"F10.wireOp",EDGE,"E145.sketch_text.stroke-302"),sQuery(id+"F10.wireOp",EDGE,"E145.sketch_text.stroke-303"),sQuery(id+"F10.wireOp",EDGE,"E145.sketch_text.stroke-304"),sQuery(id+"F10.wireOp",EDGE,"E145.sketch_text.stroke-305"),sQuery(id+"F10.wireOp",EDGE,"E145.sketch_text.stroke-306"),sQuery(id+"F10.wireOp",EDGE,"E145.sketch_text.stroke-307"),sQuery(id+"F10.wireOp",EDGE,"E145.sketch_text.stroke-308"),sQuery(id+"F10.wireOp",EDGE,"E145.sketch_text.stroke-309"),sQuery(id+"F10.wireOp",EDGE,"E145.sketch_text.stroke-310"),sQuery(id+"F10.wireOp",EDGE,"E145.sketch_text.stroke-311"),sQuery(id+"F10.wireOp",EDGE,"E145.sketch_text.stroke-312"),sQuery(id+"F10.wireOp",EDGE,"E145.sketch_text.stroke-313"),sQuery(id+"F10.wireOp",EDGE,"E145.sketch_text.stroke-314"),sQuery(id+"F10.wireOp",EDGE,"E145.sketch_text.stroke-315"),sQuery(id+"F10.wireOp",EDGE,"E145.sketch_text.stroke-316"),sQuery(id+"F10.wireOp",EDGE,"E145.sketch_text.stroke-317"),sQuery(id+"F10.wireOp",EDGE,"E145.sketch_text.stroke-318")])],"isStart":false});
            var Q12;
            Q12=makeQuery(id+"F11.opExtrude","CAP_FACE",FACE,{"disambiguationData":[OSD([sQuery(id+"F10.wireOp",EDGE,"E145.sketch_text.stroke-285"),sQuery(id+"F10.wireOp",EDGE,"E145.sketch_text.stroke-286"),sQuery(id+"F10.wireOp",EDGE,"E145.sketch_text.stroke-287"),sQuery(id+"F10.wireOp",EDGE,"E145.sketch_text.stroke-288"),sQuery(id+"F10.wireOp",EDGE,"E145.sketch_text.stroke-289"),sQuery(id+"F10.wireOp",EDGE,"E145.sketch_text.stroke-290"),sQuery(id+"F10.wireOp",EDGE,"E145.sketch_text.stroke-291"),sQuery(id+"F10.wireOp",EDGE,"E145.sketch_text.stroke-292"),sQuery(id+"F10.wireOp",EDGE,"E145.sketch_text.stroke-293")])],"isStart":false});
            var Q13;
            Q13=makeQuery(id+"F11.opExtrude","CAP_FACE",FACE,{"disambiguationData":[OSD([sQuery(id+"F10.wireOp",EDGE,"E145.sketch_text.stroke-269"),sQuery(id+"F10.wireOp",EDGE,"E145.sketch_text.stroke-270"),sQuery(id+"F10.wireOp",EDGE,"E145.sketch_text.stroke-271"),sQuery(id+"F10.wireOp",EDGE,"E145.sketch_text.stroke-272"),sQuery(id+"F10.wireOp",EDGE,"E145.sketch_text.stroke-273"),sQuery(id+"F10.wireOp",EDGE,"E145.sketch_text.stroke-274"),sQuery(id+"F10.wireOp",EDGE,"E145.sketch_text.stroke-275"),sQuery(id+"F10.wireOp",EDGE,"E145.sketch_text.stroke-276"),sQuery(id+"F10.wireOp",EDGE,"E145.sketch_text.stroke-277"),sQuery(id+"F10.wireOp",EDGE,"E145.sketch_text.stroke-278"),sQuery(id+"F10.wireOp",EDGE,"E145.sketch_text.stroke-279"),sQuery(id+"F10.wireOp",EDGE,"E145.sketch_text.stroke-280"),sQuery(id+"F10.wireOp",EDGE,"E145.sketch_text.stroke-281"),sQuery(id+"F10.wireOp",EDGE,"E145.sketch_text.stroke-282"),sQuery(id+"F10.wireOp",EDGE,"E145.sketch_text.stroke-283"),sQuery(id+"F10.wireOp",EDGE,"E145.sketch_text.stroke-284")])],"isStart":false});
            var Q14;
            Q14=makeQuery(id+"F11.opExtrude","CAP_FACE",FACE,{"disambiguationData":[OSD([sQuery(id+"F10.wireOp",EDGE,"E145.sketch_text.stroke-249"),sQuery(id+"F10.wireOp",EDGE,"E145.sketch_text.stroke-250"),sQuery(id+"F10.wireOp",EDGE,"E145.sketch_text.stroke-251"),sQuery(id+"F10.wireOp",EDGE,"E145.sketch_text.stroke-252"),sQuery(id+"F10.wireOp",EDGE,"E145.sketch_text.stroke-253"),sQuery(id+"F10.wireOp",EDGE,"E145.sketch_text.stroke-254"),sQuery(id+"F10.wireOp",EDGE,"E145.sketch_text.stroke-255"),sQuery(id+"F10.wireOp",EDGE,"E145.sketch_text.stroke-256"),sQuery(id+"F10.wireOp",EDGE,"E145.sketch_text.stroke-257"),sQuery(id+"F10.wireOp",EDGE,"E145.sketch_text.stroke-258"),sQuery(id+"F10.wireOp",EDGE,"E145.sketch_text.stroke-259"),sQuery(id+"F10.wireOp",EDGE,"E145.sketch_text.stroke-260"),sQuery(id+"F10.wireOp",EDGE,"E145.sketch_text.stroke-261"),sQuery(id+"F10.wireOp",EDGE,"E145.sketch_text.stroke-262"),sQuery(id+"F10.wireOp",EDGE,"E145.sketch_text.stroke-263"),sQuery(id+"F10.wireOp",EDGE,"E145.sketch_text.stroke-264"),sQuery(id+"F10.wireOp",EDGE,"E145.sketch_text.stroke-265"),sQuery(id+"F10.wireOp",EDGE,"E145.sketch_text.stroke-266"),sQuery(id+"F10.wireOp",EDGE,"E145.sketch_text.stroke-267"),sQuery(id+"F10.wireOp",EDGE,"E145.sketch_text.stroke-268")])],"isStart":false});
            var Q15;
            Q15=makeQuery(id+"F11.opExtrude","CAP_FACE",FACE,{"disambiguationData":[OSD([sQuery(id+"F10.wireOp",EDGE,"E145.sketch_text.stroke-241"),sQuery(id+"F10.wireOp",EDGE,"E145.sketch_text.stroke-242"),sQuery(id+"F10.wireOp",EDGE,"E145.sketch_text.stroke-243"),sQuery(id+"F10.wireOp",EDGE,"E145.sketch_text.stroke-244"),sQuery(id+"F10.wireOp",EDGE,"E145.sketch_text.stroke-245"),sQuery(id+"F10.wireOp",EDGE,"E145.sketch_text.stroke-246"),sQuery(id+"F10.wireOp",EDGE,"E145.sketch_text.stroke-247"),sQuery(id+"F10.wireOp",EDGE,"E145.sketch_text.stroke-248")])],"isStart":false});
            var Q16;
            Q16=makeQuery(id+"F11.opExtrude","CAP_FACE",FACE,{"disambiguationData":[OSD([sQuery(id+"F10.wireOp",EDGE,"E145.sketch_text.stroke-224"),sQuery(id+"F10.wireOp",EDGE,"E145.sketch_text.stroke-225"),sQuery(id+"F10.wireOp",EDGE,"E145.sketch_text.stroke-226"),sQuery(id+"F10.wireOp",EDGE,"E145.sketch_text.stroke-227"),sQuery(id+"F10.wireOp",EDGE,"E145.sketch_text.stroke-228"),sQuery(id+"F10.wireOp",EDGE,"E145.sketch_text.stroke-229"),sQuery(id+"F10.wireOp",EDGE,"E145.sketch_text.stroke-230"),sQuery(id+"F10.wireOp",EDGE,"E145.sketch_text.stroke-231"),sQuery(id+"F10.wireOp",EDGE,"E145.sketch_text.stroke-232"),sQuery(id+"F10.wireOp",EDGE,"E145.sketch_text.stroke-233"),sQuery(id+"F10.wireOp",EDGE,"E145.sketch_text.stroke-234"),sQuery(id+"F10.wireOp",EDGE,"E145.sketch_text.stroke-235"),sQuery(id+"F10.wireOp",EDGE,"E145.sketch_text.stroke-236"),sQuery(id+"F10.wireOp",EDGE,"E145.sketch_text.stroke-237"),sQuery(id+"F10.wireOp",EDGE,"E145.sketch_text.stroke-238"),sQuery(id+"F10.wireOp",EDGE,"E145.sketch_text.stroke-239"),sQuery(id+"F10.wireOp",EDGE,"E145.sketch_text.stroke-240")])],"isStart":false});
            var Q17;
            Q17=makeQuery(id+"F11.opExtrude","CAP_FACE",FACE,{"disambiguationData":[OSD([sQuery(id+"F10.wireOp",EDGE,"E145.sketch_text.stroke-209"),sQuery(id+"F10.wireOp",EDGE,"E145.sketch_text.stroke-210"),sQuery(id+"F10.wireOp",EDGE,"E145.sketch_text.stroke-211"),sQuery(id+"F10.wireOp",EDGE,"E145.sketch_text.stroke-212"),sQuery(id+"F10.wireOp",EDGE,"E145.sketch_text.stroke-213"),sQuery(id+"F10.wireOp",EDGE,"E145.sketch_text.stroke-214"),sQuery(id+"F10.wireOp",EDGE,"E145.sketch_text.stroke-215"),sQuery(id+"F10.wireOp",EDGE,"E145.sketch_text.stroke-216"),sQuery(id+"F10.wireOp",EDGE,"E145.sketch_text.stroke-217"),sQuery(id+"F10.wireOp",EDGE,"E145.sketch_text.stroke-218"),sQuery(id+"F10.wireOp",EDGE,"E145.sketch_text.stroke-219"),sQuery(id+"F10.wireOp",EDGE,"E145.sketch_text.stroke-220"),sQuery(id+"F10.wireOp",EDGE,"E145.sketch_text.stroke-221"),sQuery(id+"F10.wireOp",EDGE,"E145.sketch_text.stroke-222"),sQuery(id+"F10.wireOp",EDGE,"E145.sketch_text.stroke-223")])],"isStart":false});
            var Q18;
            Q18=makeQuery(id+"F11.opExtrude","CAP_FACE",FACE,{"disambiguationData":[OSD([sQuery(id+"F10.wireOp",EDGE,"E145.sketch_text.stroke-190"),sQuery(id+"F10.wireOp",EDGE,"E145.sketch_text.stroke-191"),sQuery(id+"F10.wireOp",EDGE,"E145.sketch_text.stroke-192"),sQuery(id+"F10.wireOp",EDGE,"E145.sketch_text.stroke-193"),sQuery(id+"F10.wireOp",EDGE,"E145.sketch_text.stroke-194"),sQuery(id+"F10.wireOp",EDGE,"E145.sketch_text.stroke-195"),sQuery(id+"F10.wireOp",EDGE,"E145.sketch_text.stroke-196"),sQuery(id+"F10.wireOp",EDGE,"E145.sketch_text.stroke-197"),sQuery(id+"F10.wireOp",EDGE,"E145.sketch_text.stroke-198"),sQuery(id+"F10.wireOp",EDGE,"E145.sketch_text.stroke-199"),sQuery(id+"F10.wireOp",EDGE,"E145.sketch_text.stroke-200"),sQuery(id+"F10.wireOp",EDGE,"E145.sketch_text.stroke-201"),sQuery(id+"F10.wireOp",EDGE,"E145.sketch_text.stroke-202"),sQuery(id+"F10.wireOp",EDGE,"E145.sketch_text.stroke-203"),sQuery(id+"F10.wireOp",EDGE,"E145.sketch_text.stroke-204"),sQuery(id+"F10.wireOp",EDGE,"E145.sketch_text.stroke-205"),sQuery(id+"F10.wireOp",EDGE,"E145.sketch_text.stroke-206"),sQuery(id+"F10.wireOp",EDGE,"E145.sketch_text.stroke-207"),sQuery(id+"F10.wireOp",EDGE,"E145.sketch_text.stroke-208")])],"isStart":false});
            extrude(context, id + "F14", {"entities" : qUnion([Q0, Q1, Q2, Q3, Q4, Q5, Q6, Q7, Q8, Q9, Q10, Q11, Q12, Q13, Q14, Q15, Q16, Q17, Q18]), "operationType" : NewBodyOperationType.REMOVE, "oppositeDirection" : true, "depth" : 2 * mm});
        }
    });
